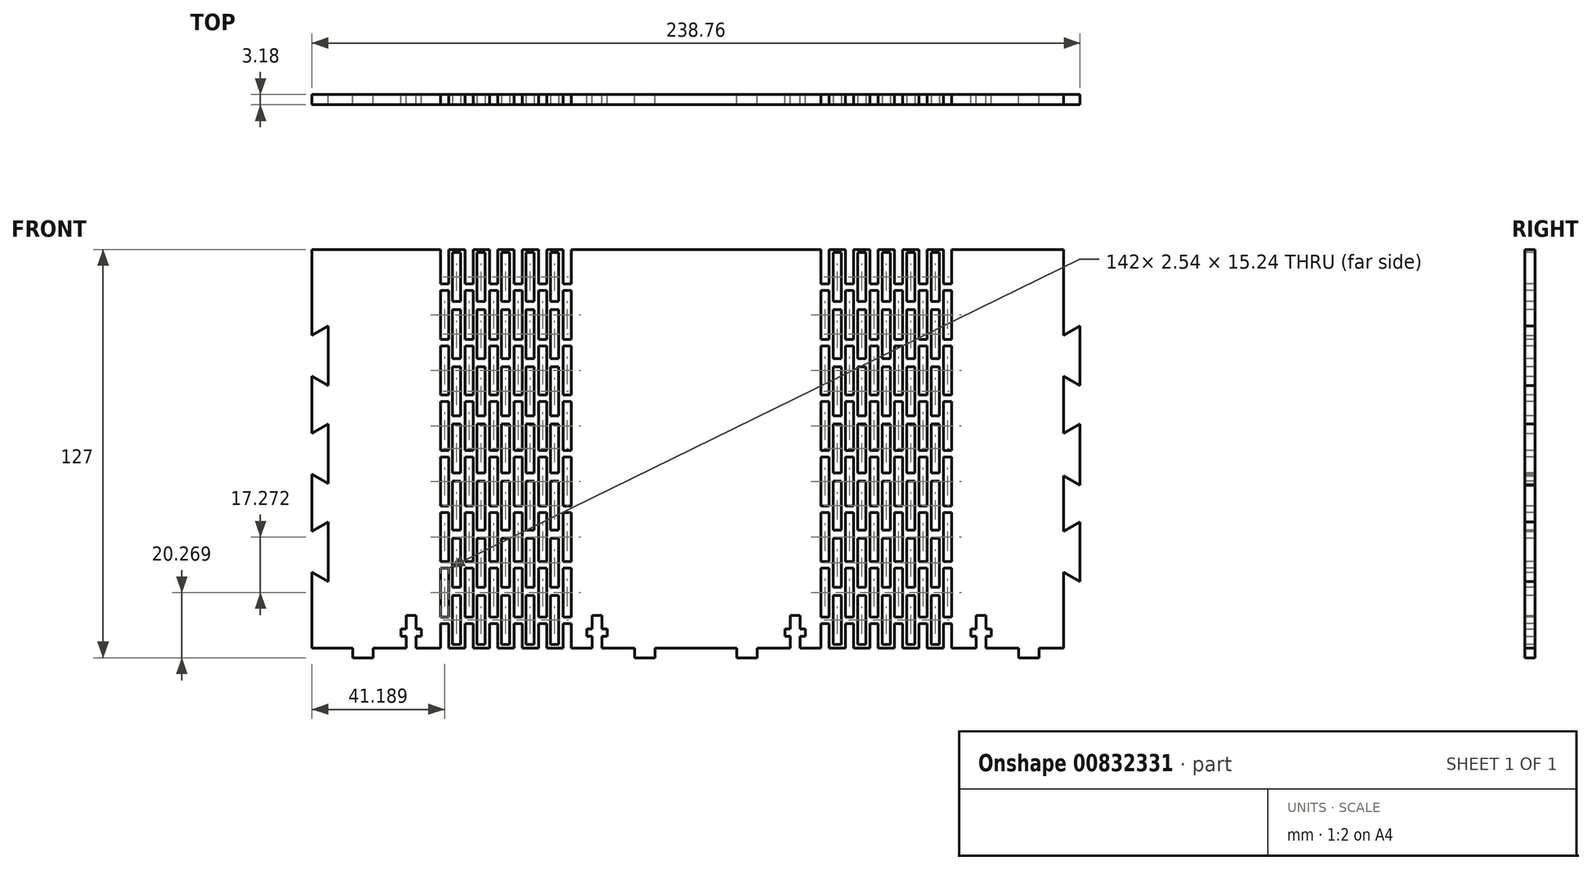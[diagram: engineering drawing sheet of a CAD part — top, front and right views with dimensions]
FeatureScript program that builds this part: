
annotation { "Feature Type Name" : "Feature", "Feature Type Description" : "" }
export const myFeature = defineFeature(function(context is Context, id is Id, definition is map)
    precondition{}
    {
        {
            var Q0;
            Q0=qCreatedBy(makeId("Front.planeOp"),FACE);
            var sketch = newSketch(context, id + "F0", { "sketchPlane" : qUnion([Q0])});
            skLineSegment(sketch, "E0.top", {"start": v(19.05, -63.5) * mm, "end": v(12.7, -63.5) * mm});
            skLineSegment(sketch, "E0.left", {"start": v(119.38, 39.76) * mm, "end": v(119.38, 21.2) * mm});
            skLineSegment(sketch, "E0.right", {"start": v(-119.38, 63.5) * mm, "end": v(-119.38, 36.83) * mm});
            skPoint(sketch, "E0.middle", {"position": v(0, 0) * mm});
            skLineSegment(sketch, "E1", {"start": v(-12.7, -60.5) * mm, "end": v(-12.7, -63.5) * mm});
            skLineSegment(sketch, "E2", {"start": v(-19.05, -60.5) * mm, "end": v(-19.05, -63.5) * mm});
            skLineSegment(sketch, "E3", {"start": v(-19.05, -60.5) * mm, "end": v(-29.26, -60.5) * mm});
            skLineSegment(sketch, "E4.MirrorCS", {"start": v(12.7, -60.5) * mm, "end": v(12.7, -63.5) * mm});
            skLineSegment(sketch, "E5.MirrorCS", {"start": v(19.05, -60.5) * mm, "end": v(19.05, -63.5) * mm});
            skLineSegment(sketch, "E6.MirrorCS", {"start": v(-19.05, -63.5) * mm, "end": v(-12.7, -63.5) * mm});
            skLineSegment(sketch, "E7.trimOffspring", {"start": v(12.7, -63.5) * mm, "end": v(19.05, -63.5) * mm});
            skLineSegment(sketch, "E8.MirrorCS", {"start": v(19.05, -60.5) * mm, "end": v(29.26, -60.5) * mm});
            skLineSegment(sketch, "E9", {"start": v(-12.7, -60.5) * mm, "end": v(12.7, -60.5) * mm});
            skLineSegment(sketch, "E10.trimOffspring", {"start": v(-12.7, -63.5) * mm, "end": v(-19.05, -63.5) * mm});
            skLineSegment(sketch, "E11.top", {"start": v(-29.26, -50.34) * mm, "end": v(-32.3, -50.34) * mm});
            skLineSegment(sketch, "E11.left", {"start": v(-29.26, -60.5) * mm, "end": v(-29.26, -56.86) * mm});
            skLineSegment(sketch, "E11.right", {"start": v(-32.3, -60.5) * mm, "end": v(-32.3, -56.86) * mm});
            skLineSegment(sketch, "E12", {"start": v(-30.78, -61.4) * mm, "end": v(-30.78, -30.9) * mm, "construction": true});
            skPoint(sketch, "E12.startSnap0", {"position": v(-30.78, -50.34) * mm});
            skLineSegment(sketch, "E13.bottom", {"start": v(-27.6, -54.48) * mm, "end": v(-29.26, -54.48) * mm});
            skLineSegment(sketch, "E13.top", {"start": v(-27.6, -56.86) * mm, "end": v(-29.26, -56.86) * mm});
            skLineSegment(sketch, "E13.left", {"start": v(-27.6, -54.48) * mm, "end": v(-27.6, -56.86) * mm});
            skLineSegment(sketch, "E13.right", {"start": v(-33.96, -54.48) * mm, "end": v(-33.96, -56.86) * mm});
            skPoint(sketch, "E13.middle", {"position": v(-30.78, -55.67) * mm});
            skLineSegment(sketch, "E14.trimOffspring", {"start": v(-32.3, -54.48) * mm, "end": v(-32.3, -50.34) * mm});
            skLineSegment(sketch, "E15.trimOffspring", {"start": v(-32.3, -54.48) * mm, "end": v(-33.96, -54.48) * mm});
            skLineSegment(sketch, "E16.trimOffspring", {"start": v(-32.3, -56.86) * mm, "end": v(-33.96, -56.86) * mm});
            skLineSegment(sketch, "E17.trimOffspring", {"start": v(-29.26, -54.48) * mm, "end": v(-29.26, -50.34) * mm});
            skLineSegment(sketch, "E18.MirrorCS", {"start": v(29.26, -60.5) * mm, "end": v(29.26, -56.86) * mm});
            skLineSegment(sketch, "E19.MirrorCS", {"start": v(27.6, -56.86) * mm, "end": v(29.26, -56.86) * mm});
            skLineSegment(sketch, "E20.MirrorCS", {"start": v(27.6, -54.48) * mm, "end": v(27.6, -56.86) * mm});
            skLineSegment(sketch, "E21.MirrorCS", {"start": v(27.6, -54.48) * mm, "end": v(29.26, -54.48) * mm});
            skLineSegment(sketch, "E22.MirrorCS", {"start": v(32.3, -60.5) * mm, "end": v(32.3, -56.86) * mm});
            skLineSegment(sketch, "E23.MirrorCS", {"start": v(32.3, -56.86) * mm, "end": v(33.96, -56.86) * mm});
            skLineSegment(sketch, "E24.MirrorCS", {"start": v(33.96, -54.48) * mm, "end": v(33.96, -56.86) * mm});
            skLineSegment(sketch, "E25.MirrorCS", {"start": v(32.3, -54.48) * mm, "end": v(33.96, -54.48) * mm});
            skLineSegment(sketch, "E26.MirrorCS", {"start": v(32.3, -54.48) * mm, "end": v(32.3, -50.34) * mm});
            skLineSegment(sketch, "E27.MirrorCS", {"start": v(29.26, -50.34) * mm, "end": v(32.3, -50.34) * mm});
            skLineSegment(sketch, "E28.MirrorCS", {"start": v(29.26, -54.48) * mm, "end": v(29.26, -50.34) * mm});
            skLineSegment(sketch, "E29.trimOffspring", {"start": v(32.3, -60.5) * mm, "end": v(87.07, -60.5) * mm});
            skLineSegment(sketch, "E30.MirrorCS", {"start": v(114.3, 63.5) * mm, "end": v(114.3, -66.28) * mm, "construction": true});
            skLineSegment(sketch, "E31", {"start": v(-119.38, 6.35) * mm, "end": v(-114.3, 9.28) * mm});
            skLineSegment(sketch, "E32.MirrorCS", {"start": v(-119.38, -6.35) * mm, "end": v(-114.3, -9.28) * mm});
            skPoint(sketch, "E33", {"position": v(-114.3, -1.4) * mm});
            skLineSegment(sketch, "E34.0.1.0", {"start": v(-119.38, 36.83) * mm, "end": v(-114.3, 39.76) * mm});
            skLineSegment(sketch, "E34.0.1.1", {"start": v(-119.38, 24.13) * mm, "end": v(-114.3, 21.2) * mm});
            skLineSegment(sketch, "E34.direction1", {"start": v(-119.38, 6.35) * mm, "end": v(-93.98, 6.35) * mm, "construction": true});
            skLineSegment(sketch, "E35.MirrorCS", {"start": v(-100.33, -60.5) * mm, "end": v(-100.33, -63.5) * mm});
            skLineSegment(sketch, "E36.MirrorCS", {"start": v(-106.68, -63.5) * mm, "end": v(-100.33, -63.5) * mm});
            skLineSegment(sketch, "E37.MirrorCS", {"start": v(-106.68, -60.5) * mm, "end": v(-106.68, -63.5) * mm});
            skLineSegment(sketch, "E38.MirrorCS", {"start": v(-90.12, -60.5) * mm, "end": v(-90.12, -56.86) * mm});
            skLineSegment(sketch, "E39.MirrorCS", {"start": v(-87.07, -60.5) * mm, "end": v(-87.07, -56.86) * mm});
            skLineSegment(sketch, "E40.MirrorCS", {"start": v(-87.07, -56.86) * mm, "end": v(-85.42, -56.86) * mm});
            skLineSegment(sketch, "E41.MirrorCS", {"start": v(-85.42, -54.48) * mm, "end": v(-85.42, -56.86) * mm});
            skLineSegment(sketch, "E42.MirrorCS", {"start": v(-87.07, -54.48) * mm, "end": v(-85.42, -54.48) * mm});
            skLineSegment(sketch, "E43.MirrorCS", {"start": v(-87.07, -54.48) * mm, "end": v(-87.07, -50.34) * mm});
            skLineSegment(sketch, "E44.MirrorCS", {"start": v(-90.12, -50.34) * mm, "end": v(-87.07, -50.34) * mm});
            skLineSegment(sketch, "E45.MirrorCS", {"start": v(-90.12, -54.48) * mm, "end": v(-90.12, -50.34) * mm});
            skLineSegment(sketch, "E46.MirrorCS", {"start": v(-91.77, -54.48) * mm, "end": v(-90.12, -54.48) * mm});
            skLineSegment(sketch, "E47.MirrorCS", {"start": v(-91.77, -54.48) * mm, "end": v(-91.77, -56.86) * mm});
            skLineSegment(sketch, "E48.MirrorCS", {"start": v(-91.77, -56.86) * mm, "end": v(-90.12, -56.86) * mm});
            skLineSegment(sketch, "E49.trimOffspring", {"start": v(-90.12, -60.5) * mm, "end": v(-100.33, -60.5) * mm});
            skLineSegment(sketch, "E50.trimOffspring", {"start": v(-106.68, -60.5) * mm, "end": v(-119.38, -60.5) * mm});
            skLineSegment(sketch, "E51.MirrorCS", {"start": v(-119.38, -24.13) * mm, "end": v(-114.3, -21.2) * mm});
            skLineSegment(sketch, "E52.MirrorCS", {"start": v(-119.38, -36.83) * mm, "end": v(-114.3, -39.76) * mm});
            skLineSegment(sketch, "E53", {"start": v(-114.3, 39.76) * mm, "end": v(-114.3, 21.2) * mm});
            skLineSegment(sketch, "E54", {"start": v(-114.3, -39.76) * mm, "end": v(-114.3, -21.2) * mm});
            skLineSegment(sketch, "E55", {"start": v(-114.3, 9.28) * mm, "end": v(-114.3, -9.28) * mm});
            skLineSegment(sketch, "E56.trimOffspring", {"start": v(-119.38, 24.13) * mm, "end": v(-119.38, 6.35) * mm});
            skLineSegment(sketch, "E57.trimOffspring", {"start": v(-119.38, -6.35) * mm, "end": v(-119.38, -24.13) * mm});
            skLineSegment(sketch, "E58.trimOffspring", {"start": v(-119.38, -36.83) * mm, "end": v(-119.38, -60.5) * mm});
            skLineSegment(sketch, "E59.1.0.0", {"start": v(114.3, 36.83) * mm, "end": v(119.38, 39.76) * mm});
            skLineSegment(sketch, "E59.1.0.2", {"start": v(114.3, 24.13) * mm, "end": v(119.38, 21.2) * mm});
            skLineSegment(sketch, "E59.direction1", {"start": v(-119.38, 36.83) * mm, "end": v(114.3, 36.83) * mm, "construction": true});
            skLineSegment(sketch, "E60", {"start": v(114.3, 36.83) * mm, "end": v(114.3, 63.5) * mm});
            skLineSegment(sketch, "E61.1.0.0", {"start": v(114.3, 6.35) * mm, "end": v(119.38, 9.28) * mm});
            skLineSegment(sketch, "E61.1.0.1", {"start": v(119.38, 9.28) * mm, "end": v(119.38, -9.28) * mm});
            skLineSegment(sketch, "E61.1.0.2", {"start": v(114.3, -6.96) * mm, "end": v(119.38, -9.9) * mm});
            skLineSegment(sketch, "E61.direction1", {"start": v(-119.38, 6.35) * mm, "end": v(114.3, 6.35) * mm, "construction": true});
            skLineSegment(sketch, "E62", {"start": v(114.3, 24.13) * mm, "end": v(114.3, 6.35) * mm});
            skLineSegment(sketch, "E63.1.0.0", {"start": v(119.38, -39.76) * mm, "end": v(119.38, -21.2) * mm});
            skLineSegment(sketch, "E63.1.0.1", {"start": v(114.3, -24.13) * mm, "end": v(119.38, -21.2) * mm});
            skLineSegment(sketch, "E63.1.0.2", {"start": v(114.3, -36.83) * mm, "end": v(119.38, -39.76) * mm});
            skLineSegment(sketch, "E63.direction1", {"start": v(-114.3, -39.76) * mm, "end": v(119.38, -39.76) * mm, "construction": true});
            skLineSegment(sketch, "E64", {"start": v(114.3, -24.13) * mm, "end": v(114.3, -6.96) * mm});
            skLineSegment(sketch, "E65", {"start": v(114.3, -60.5) * mm, "end": v(114.3, -36.83) * mm});
            skLineSegment(sketch, "E66.trimOffspring", {"start": v(119.38, -21.2) * mm, "end": v(119.38, -39.76) * mm});
            skLineSegment(sketch, "E67.MirrorCS", {"start": v(87.07, -60.5) * mm, "end": v(87.07, -56.86) * mm});
            skLineSegment(sketch, "E68.MirrorCS", {"start": v(87.07, -56.86) * mm, "end": v(85.42, -56.86) * mm});
            skLineSegment(sketch, "E69.MirrorCS", {"start": v(85.42, -54.48) * mm, "end": v(85.42, -56.86) * mm});
            skLineSegment(sketch, "E70.MirrorCS", {"start": v(87.07, -54.48) * mm, "end": v(85.42, -54.48) * mm});
            skLineSegment(sketch, "E71.MirrorCS", {"start": v(87.07, -54.48) * mm, "end": v(87.07, -50.34) * mm});
            skLineSegment(sketch, "E72.MirrorCS", {"start": v(90.12, -50.34) * mm, "end": v(87.07, -50.34) * mm});
            skLineSegment(sketch, "E73.MirrorCS", {"start": v(90.12, -54.48) * mm, "end": v(90.12, -50.34) * mm});
            skLineSegment(sketch, "E74.MirrorCS", {"start": v(91.77, -54.48) * mm, "end": v(90.12, -54.48) * mm});
            skLineSegment(sketch, "E75.MirrorCS", {"start": v(91.77, -54.48) * mm, "end": v(91.77, -56.86) * mm});
            skLineSegment(sketch, "E76.MirrorCS", {"start": v(91.77, -56.86) * mm, "end": v(90.12, -56.86) * mm});
            skLineSegment(sketch, "E77.MirrorCS", {"start": v(90.12, -60.5) * mm, "end": v(90.12, -56.86) * mm});
            skLineSegment(sketch, "E78.MirrorCS", {"start": v(106.68, -60.5) * mm, "end": v(106.68, -63.5) * mm});
            skLineSegment(sketch, "E79.MirrorCS", {"start": v(106.68, -63.5) * mm, "end": v(100.33, -63.5) * mm});
            skLineSegment(sketch, "E80.MirrorCS", {"start": v(100.33, -60.5) * mm, "end": v(100.33, -63.5) * mm});
            skLineSegment(sketch, "E81.trimOffspring", {"start": v(90.12, -60.5) * mm, "end": v(100.33, -60.5) * mm});
            skLineSegment(sketch, "E82.trimOffspring", {"start": v(106.68, -60.5) * mm, "end": v(114.3, -60.5) * mm});
            skLineSegment(sketch, "E83", {"start": v(119.38, -9.9) * mm, "end": v(119.38, -9.28) * mm});
            skLineSegment(sketch, "E84", {"start": v(-87.07, -60.5) * mm, "end": v(-32.3, -60.5) * mm});
            skLineSegment(sketch, "E85", {"start": v(-119.38, 63.5) * mm, "end": v(114.3, 63.5) * mm});
            skSolve(sketch);
        }
        {
            var Q0;
            Q0 = qSketchRegion(id + "F0", true);
            extrude(context, id + "F1", {"entities" : qUnion([Q0]), "depth" : 3.17 * mm, "offsetDistance" : 25.4 * mm});
        }
        {
            var Q0;
            Q0=makeQuery(id+"F1.opExtrude","CAP_FACE",FACE,{"disambiguationData":[OSD([sQuery(id+"F0.wireOp",EDGE,"E0.right"),sQuery(id+"F0.wireOp",EDGE,"E1"),sQuery(id+"F0.wireOp",EDGE,"E2"),sQuery(id+"F0.wireOp",EDGE,"E3"),sQuery(id+"F0.wireOp",EDGE,"E4.MirrorCS"),sQuery(id+"F0.wireOp",EDGE,"E5.MirrorCS"),sQuery(id+"F0.wireOp",EDGE,"E7.trimOffspring"),sQuery(id+"F0.wireOp",EDGE,"E8.MirrorCS"),sQuery(id+"F0.wireOp",EDGE,"E9"),sQuery(id+"F0.wireOp",EDGE,"E10.trimOffspring"),sQuery(id+"F0.wireOp",EDGE,"E11.top"),sQuery(id+"F0.wireOp",EDGE,"E11.left"),sQuery(id+"F0.wireOp",EDGE,"E11.right"),sQuery(id+"F0.wireOp",EDGE,"E13.bottom"),sQuery(id+"F0.wireOp",EDGE,"E13.top"),sQuery(id+"F0.wireOp",EDGE,"E13.left"),sQuery(id+"F0.wireOp",EDGE,"E13.right"),sQuery(id+"F0.wireOp",EDGE,"E14.trimOffspring"),sQuery(id+"F0.wireOp",EDGE,"E15.trimOffspring"),sQuery(id+"F0.wireOp",EDGE,"E16.trimOffspring"),sQuery(id+"F0.wireOp",EDGE,"E17.trimOffspring"),sQuery(id+"F0.wireOp",EDGE,"E18.MirrorCS"),sQuery(id+"F0.wireOp",EDGE,"E19.MirrorCS"),sQuery(id+"F0.wireOp",EDGE,"E20.MirrorCS"),sQuery(id+"F0.wireOp",EDGE,"E21.MirrorCS"),sQuery(id+"F0.wireOp",EDGE,"E22.MirrorCS"),sQuery(id+"F0.wireOp",EDGE,"E23.MirrorCS"),sQuery(id+"F0.wireOp",EDGE,"E24.MirrorCS"),sQuery(id+"F0.wireOp",EDGE,"E25.MirrorCS"),sQuery(id+"F0.wireOp",EDGE,"E26.MirrorCS"),sQuery(id+"F0.wireOp",EDGE,"E27.MirrorCS"),sQuery(id+"F0.wireOp",EDGE,"E28.MirrorCS"),sQuery(id+"F0.wireOp",EDGE,"E29.trimOffspring"),sQuery(id+"F0.wireOp",EDGE,"E31"),sQuery(id+"F0.wireOp",EDGE,"E32.MirrorCS"),sQuery(id+"F0.wireOp",EDGE,"E34.0.1.0"),sQuery(id+"F0.wireOp",EDGE,"E34.0.1.1"),sQuery(id+"F0.wireOp",EDGE,"E35.MirrorCS"),sQuery(id+"F0.wireOp",EDGE,"E36.MirrorCS"),sQuery(id+"F0.wireOp",EDGE,"E37.MirrorCS"),sQuery(id+"F0.wireOp",EDGE,"E39.MirrorCS"),sQuery(id+"F0.wireOp",EDGE,"E40.MirrorCS"),sQuery(id+"F0.wireOp",EDGE,"E41.MirrorCS"),sQuery(id+"F0.wireOp",EDGE,"E42.MirrorCS"),sQuery(id+"F0.wireOp",EDGE,"E43.MirrorCS"),sQuery(id+"F0.wireOp",EDGE,"E44.MirrorCS"),sQuery(id+"F0.wireOp",EDGE,"E45.MirrorCS"),sQuery(id+"F0.wireOp",EDGE,"E46.MirrorCS"),sQuery(id+"F0.wireOp",EDGE,"E47.MirrorCS"),sQuery(id+"F0.wireOp",EDGE,"E48.MirrorCS"),sQuery(id+"F0.wireOp",EDGE,"E38.MirrorCS"),sQuery(id+"F0.wireOp",EDGE,"E49.trimOffspring"),sQuery(id+"F0.wireOp",EDGE,"E50.trimOffspring"),sQuery(id+"F0.wireOp",EDGE,"E51.MirrorCS"),sQuery(id+"F0.wireOp",EDGE,"E52.MirrorCS"),sQuery(id+"F0.wireOp",EDGE,"E53"),sQuery(id+"F0.wireOp",EDGE,"E54"),sQuery(id+"F0.wireOp",EDGE,"E55"),sQuery(id+"F0.wireOp",EDGE,"E56.trimOffspring"),sQuery(id+"F0.wireOp",EDGE,"E57.trimOffspring"),sQuery(id+"F0.wireOp",EDGE,"E58.trimOffspring"),sQuery(id+"F0.wireOp",EDGE,"E59.1.0.0"),sQuery(id+"F0.wireOp",EDGE,"E0.left"),sQuery(id+"F0.wireOp",EDGE,"E59.1.0.2"),sQuery(id+"F0.wireOp",EDGE,"E60"),sQuery(id+"F0.wireOp",EDGE,"E61.1.0.0"),sQuery(id+"F0.wireOp",EDGE,"E61.1.0.2"),sQuery(id+"F0.wireOp",EDGE,"E62"),sQuery(id+"F0.wireOp",EDGE,"E61.1.0.1"),sQuery(id+"F0.wireOp",EDGE,"E63.1.0.1"),sQuery(id+"F0.wireOp",EDGE,"E63.1.0.2"),sQuery(id+"F0.wireOp",EDGE,"E64"),sQuery(id+"F0.wireOp",EDGE,"E65"),sQuery(id+"F0.wireOp",EDGE,"E66.trimOffspring"),sQuery(id+"F0.wireOp",EDGE,"E67.MirrorCS"),sQuery(id+"F0.wireOp",EDGE,"E68.MirrorCS"),sQuery(id+"F0.wireOp",EDGE,"E69.MirrorCS"),sQuery(id+"F0.wireOp",EDGE,"E70.MirrorCS"),sQuery(id+"F0.wireOp",EDGE,"E71.MirrorCS"),sQuery(id+"F0.wireOp",EDGE,"E72.MirrorCS"),sQuery(id+"F0.wireOp",EDGE,"E73.MirrorCS"),sQuery(id+"F0.wireOp",EDGE,"E74.MirrorCS"),sQuery(id+"F0.wireOp",EDGE,"E75.MirrorCS"),sQuery(id+"F0.wireOp",EDGE,"E76.MirrorCS"),sQuery(id+"F0.wireOp",EDGE,"E77.MirrorCS"),sQuery(id+"F0.wireOp",EDGE,"E78.MirrorCS"),sQuery(id+"F0.wireOp",EDGE,"E79.MirrorCS"),sQuery(id+"F0.wireOp",EDGE,"E80.MirrorCS"),sQuery(id+"F0.wireOp",EDGE,"E81.trimOffspring"),sQuery(id+"F0.wireOp",EDGE,"E82.trimOffspring"),sQuery(id+"F0.wireOp",EDGE,"E83"),sQuery(id+"F0.wireOp",EDGE,"E84"),sQuery(id+"F0.wireOp",EDGE,"E85")])],"isStart":false});
            var sketch = newSketch(context, id + "F2", { "sketchPlane" : qUnion([Q0])});
            skLineSegment(sketch, "E86", {"start": v(-38.22, -63.67) * mm, "end": v(-38.22, 65.15) * mm, "construction": true});
            skLineSegment(sketch, "E87.1.0.0", {"start": v(-42.03, -63.67) * mm, "end": v(-42.03, 65.15) * mm, "construction": true});
            skLineSegment(sketch, "E87.2.0.0", {"start": v(-45.84, -63.67) * mm, "end": v(-45.84, 65.15) * mm, "construction": true});
            skLineSegment(sketch, "E87.3.0.0", {"start": v(-49.65, -63.67) * mm, "end": v(-49.65, 65.15) * mm, "construction": true});
            skLineSegment(sketch, "E87.4.0.0", {"start": v(-53.46, -63.67) * mm, "end": v(-53.46, 65.15) * mm, "construction": true});
            skLineSegment(sketch, "E87.5.0.0", {"start": v(-57.27, -63.67) * mm, "end": v(-57.27, 65.15) * mm, "construction": true});
            skLineSegment(sketch, "E87.6.0.0", {"start": v(-61.08, -63.67) * mm, "end": v(-61.08, 65.15) * mm, "construction": true});
            skLineSegment(sketch, "E87.7.0.0", {"start": v(-64.89, -63.67) * mm, "end": v(-64.89, 65.15) * mm, "construction": true});
            skLineSegment(sketch, "E87.8.0.0", {"start": v(-68.7, -63.67) * mm, "end": v(-68.7, 65.15) * mm, "construction": true});
            skLineSegment(sketch, "E87.9.0.0", {"start": v(-72.5, -63.67) * mm, "end": v(-72.5, 65.15) * mm, "construction": true});
            skLineSegment(sketch, "E87.10.0.0", {"start": v(-76.32, -63.67) * mm, "end": v(-76.32, 65.15) * mm, "construction": true});
            skLineSegment(sketch, "E87.11.0.0", {"start": v(-80.13, -63.67) * mm, "end": v(-80.13, 65.15) * mm, "construction": true});
            skLineSegment(sketch, "E87.direction1", {"start": v(-38.22, -63.67) * mm, "end": v(-42.03, -63.67) * mm, "construction": true});
            skLineSegment(sketch, "E88.bottom", {"start": v(-38.82, -52.88) * mm, "end": v(-41.36, -52.88) * mm});
            skLineSegment(sketch, "E88.left", {"start": v(-38.82, -52.88) * mm, "end": v(-38.82, -60.5) * mm});
            skLineSegment(sketch, "E88.right", {"start": v(-41.36, -52.88) * mm, "end": v(-41.36, -60.5) * mm});
            skPoint(sketch, "E88.middle", {"position": v(-40.1, -60.5) * mm});
            skLineSegment(sketch, "E89.0.1.0", {"start": v(-38.82, -35.61) * mm, "end": v(-38.82, -50.85) * mm});
            skPoint(sketch, "E89.0.1.1", {"position": v(-40.1, -43.23) * mm});
            skLineSegment(sketch, "E89.0.1.2", {"start": v(-38.82, -50.85) * mm, "end": v(-41.36, -50.85) * mm});
            skLineSegment(sketch, "E89.0.1.3", {"start": v(-38.82, -35.61) * mm, "end": v(-41.36, -35.61) * mm});
            skLineSegment(sketch, "E89.0.1.4", {"start": v(-41.36, -35.61) * mm, "end": v(-41.36, -50.85) * mm});
            skLineSegment(sketch, "E89.0.2.0", {"start": v(-38.82, -18.34) * mm, "end": v(-38.82, -33.58) * mm});
            skPoint(sketch, "E89.0.2.1", {"position": v(-40.1, -25.96) * mm});
            skLineSegment(sketch, "E89.0.2.2", {"start": v(-38.82, -33.58) * mm, "end": v(-41.36, -33.58) * mm});
            skLineSegment(sketch, "E89.0.2.3", {"start": v(-38.82, -18.34) * mm, "end": v(-41.36, -18.34) * mm});
            skLineSegment(sketch, "E89.0.2.4", {"start": v(-41.36, -18.34) * mm, "end": v(-41.36, -33.58) * mm});
            skLineSegment(sketch, "E89.0.3.0", {"start": v(-38.82, -1.07) * mm, "end": v(-38.82, -16.3) * mm});
            skPoint(sketch, "E89.0.3.1", {"position": v(-40.1, -8.69) * mm});
            skLineSegment(sketch, "E89.0.3.2", {"start": v(-38.82, -16.3) * mm, "end": v(-41.36, -16.3) * mm});
            skLineSegment(sketch, "E89.0.3.3", {"start": v(-38.82, -1.07) * mm, "end": v(-41.36, -1.07) * mm});
            skLineSegment(sketch, "E89.0.3.4", {"start": v(-41.36, -1.07) * mm, "end": v(-41.36, -16.3) * mm});
            skLineSegment(sketch, "E89.0.4.0", {"start": v(-38.82, 16.2) * mm, "end": v(-38.82, 0.97) * mm});
            skPoint(sketch, "E89.0.4.1", {"position": v(-40.1, 8.59) * mm});
            skLineSegment(sketch, "E89.0.4.2", {"start": v(-38.82, 0.97) * mm, "end": v(-41.36, 0.97) * mm});
            skLineSegment(sketch, "E89.0.4.3", {"start": v(-38.82, 16.2) * mm, "end": v(-41.36, 16.2) * mm});
            skLineSegment(sketch, "E89.0.4.4", {"start": v(-41.36, 16.2) * mm, "end": v(-41.36, 0.97) * mm});
            skLineSegment(sketch, "E89.0.5.0", {"start": v(-38.82, 33.48) * mm, "end": v(-38.82, 18.24) * mm});
            skPoint(sketch, "E89.0.5.1", {"position": v(-40.1, 25.86) * mm});
            skLineSegment(sketch, "E89.0.5.2", {"start": v(-38.82, 18.24) * mm, "end": v(-41.36, 18.24) * mm});
            skLineSegment(sketch, "E89.0.5.3", {"start": v(-38.82, 33.48) * mm, "end": v(-41.36, 33.48) * mm});
            skLineSegment(sketch, "E89.0.5.4", {"start": v(-41.36, 33.48) * mm, "end": v(-41.36, 18.24) * mm});
            skLineSegment(sketch, "E89.0.6.0", {"start": v(-38.82, 50.75) * mm, "end": v(-38.82, 35.5) * mm});
            skPoint(sketch, "E89.0.6.1", {"position": v(-40.1, 43.13) * mm});
            skLineSegment(sketch, "E89.0.6.2", {"start": v(-38.82, 35.5) * mm, "end": v(-41.36, 35.5) * mm});
            skLineSegment(sketch, "E89.0.6.3", {"start": v(-38.82, 50.75) * mm, "end": v(-41.36, 50.75) * mm});
            skLineSegment(sketch, "E89.0.6.4", {"start": v(-41.36, 50.75) * mm, "end": v(-41.36, 35.5) * mm});
            skLineSegment(sketch, "E89.0.7.0", {"start": v(-38.82, 63.5) * mm, "end": v(-38.82, 52.78) * mm});
            skPoint(sketch, "E89.0.7.1", {"position": v(-40.1, 60.4) * mm});
            skLineSegment(sketch, "E89.0.7.2", {"start": v(-38.82, 52.78) * mm, "end": v(-41.36, 52.78) * mm});
            skLineSegment(sketch, "E89.0.7.4", {"start": v(-41.36, 63.5) * mm, "end": v(-41.36, 52.78) * mm});
            skLineSegment(sketch, "E89.1.0.0", {"start": v(-46.44, -52.88) * mm, "end": v(-46.44, -60.5) * mm});
            skPoint(sketch, "E89.1.0.1", {"position": v(-47.71, -60.5) * mm});
            skLineSegment(sketch, "E89.1.0.3", {"start": v(-46.44, -52.88) * mm, "end": v(-48.98, -52.88) * mm});
            skLineSegment(sketch, "E89.1.0.4", {"start": v(-48.98, -52.88) * mm, "end": v(-48.98, -60.5) * mm});
            skLineSegment(sketch, "E89.1.1.0", {"start": v(-46.44, -35.61) * mm, "end": v(-46.44, -50.85) * mm});
            skPoint(sketch, "E89.1.1.1", {"position": v(-47.71, -43.23) * mm});
            skLineSegment(sketch, "E89.1.1.2", {"start": v(-46.44, -50.85) * mm, "end": v(-48.98, -50.85) * mm});
            skLineSegment(sketch, "E89.1.1.3", {"start": v(-46.44, -35.61) * mm, "end": v(-48.98, -35.61) * mm});
            skLineSegment(sketch, "E89.1.1.4", {"start": v(-48.98, -35.61) * mm, "end": v(-48.98, -50.85) * mm});
            skLineSegment(sketch, "E89.1.2.0", {"start": v(-46.44, -18.34) * mm, "end": v(-46.44, -33.58) * mm});
            skPoint(sketch, "E89.1.2.1", {"position": v(-47.71, -25.96) * mm});
            skLineSegment(sketch, "E89.1.2.2", {"start": v(-46.44, -33.58) * mm, "end": v(-48.98, -33.58) * mm});
            skLineSegment(sketch, "E89.1.2.3", {"start": v(-46.44, -18.34) * mm, "end": v(-48.98, -18.34) * mm});
            skLineSegment(sketch, "E89.1.2.4", {"start": v(-48.98, -18.34) * mm, "end": v(-48.98, -33.58) * mm});
            skLineSegment(sketch, "E89.1.3.0", {"start": v(-46.44, -1.07) * mm, "end": v(-46.44, -16.3) * mm});
            skPoint(sketch, "E89.1.3.1", {"position": v(-47.71, -8.69) * mm});
            skLineSegment(sketch, "E89.1.3.2", {"start": v(-46.44, -16.3) * mm, "end": v(-48.98, -16.3) * mm});
            skLineSegment(sketch, "E89.1.3.3", {"start": v(-46.44, -1.07) * mm, "end": v(-48.98, -1.07) * mm});
            skLineSegment(sketch, "E89.1.3.4", {"start": v(-48.98, -1.07) * mm, "end": v(-48.98, -16.3) * mm});
            skLineSegment(sketch, "E89.1.4.0", {"start": v(-46.44, 16.2) * mm, "end": v(-46.44, 0.97) * mm});
            skPoint(sketch, "E89.1.4.1", {"position": v(-47.71, 8.59) * mm});
            skLineSegment(sketch, "E89.1.4.2", {"start": v(-46.44, 0.97) * mm, "end": v(-48.98, 0.97) * mm});
            skLineSegment(sketch, "E89.1.4.3", {"start": v(-46.44, 16.2) * mm, "end": v(-48.98, 16.2) * mm});
            skLineSegment(sketch, "E89.1.4.4", {"start": v(-48.98, 16.2) * mm, "end": v(-48.98, 0.97) * mm});
            skLineSegment(sketch, "E89.1.5.0", {"start": v(-46.44, 33.48) * mm, "end": v(-46.44, 18.24) * mm});
            skPoint(sketch, "E89.1.5.1", {"position": v(-47.71, 25.86) * mm});
            skLineSegment(sketch, "E89.1.5.2", {"start": v(-46.44, 18.24) * mm, "end": v(-48.98, 18.24) * mm});
            skLineSegment(sketch, "E89.1.5.3", {"start": v(-46.44, 33.48) * mm, "end": v(-48.98, 33.48) * mm});
            skLineSegment(sketch, "E89.1.5.4", {"start": v(-48.98, 33.48) * mm, "end": v(-48.98, 18.24) * mm});
            skLineSegment(sketch, "E89.1.6.0", {"start": v(-46.44, 50.75) * mm, "end": v(-46.44, 35.5) * mm});
            skPoint(sketch, "E89.1.6.1", {"position": v(-47.71, 43.13) * mm});
            skLineSegment(sketch, "E89.1.6.2", {"start": v(-46.44, 35.5) * mm, "end": v(-48.98, 35.5) * mm});
            skLineSegment(sketch, "E89.1.6.3", {"start": v(-46.44, 50.75) * mm, "end": v(-48.98, 50.75) * mm});
            skLineSegment(sketch, "E89.1.6.4", {"start": v(-48.98, 50.75) * mm, "end": v(-48.98, 35.5) * mm});
            skLineSegment(sketch, "E89.1.7.0", {"start": v(-46.44, 63.5) * mm, "end": v(-46.44, 52.78) * mm});
            skPoint(sketch, "E89.1.7.1", {"position": v(-47.71, 60.4) * mm});
            skLineSegment(sketch, "E89.1.7.2", {"start": v(-46.44, 52.78) * mm, "end": v(-48.98, 52.78) * mm});
            skLineSegment(sketch, "E89.1.7.4", {"start": v(-48.98, 63.5) * mm, "end": v(-48.98, 52.78) * mm});
            skLineSegment(sketch, "E89.2.0.0", {"start": v(-54.06, -52.88) * mm, "end": v(-54.06, -60.5) * mm});
            skPoint(sketch, "E89.2.0.1", {"position": v(-55.33, -60.5) * mm});
            skLineSegment(sketch, "E89.2.0.3", {"start": v(-54.06, -52.88) * mm, "end": v(-56.6, -52.88) * mm});
            skLineSegment(sketch, "E89.2.0.4", {"start": v(-56.6, -52.88) * mm, "end": v(-56.6, -60.5) * mm});
            skLineSegment(sketch, "E89.2.1.0", {"start": v(-54.06, -35.61) * mm, "end": v(-54.06, -50.85) * mm});
            skPoint(sketch, "E89.2.1.1", {"position": v(-55.33, -43.23) * mm});
            skLineSegment(sketch, "E89.2.1.2", {"start": v(-54.06, -50.85) * mm, "end": v(-56.6, -50.85) * mm});
            skLineSegment(sketch, "E89.2.1.3", {"start": v(-54.06, -35.61) * mm, "end": v(-56.6, -35.61) * mm});
            skLineSegment(sketch, "E89.2.1.4", {"start": v(-56.6, -35.61) * mm, "end": v(-56.6, -50.85) * mm});
            skLineSegment(sketch, "E89.2.2.0", {"start": v(-54.06, -18.34) * mm, "end": v(-54.06, -33.58) * mm});
            skPoint(sketch, "E89.2.2.1", {"position": v(-55.33, -25.96) * mm});
            skLineSegment(sketch, "E89.2.2.2", {"start": v(-54.06, -33.58) * mm, "end": v(-56.6, -33.58) * mm});
            skLineSegment(sketch, "E89.2.2.3", {"start": v(-54.06, -18.34) * mm, "end": v(-56.6, -18.34) * mm});
            skLineSegment(sketch, "E89.2.2.4", {"start": v(-56.6, -18.34) * mm, "end": v(-56.6, -33.58) * mm});
            skLineSegment(sketch, "E89.2.3.0", {"start": v(-54.06, -1.07) * mm, "end": v(-54.06, -16.3) * mm});
            skPoint(sketch, "E89.2.3.1", {"position": v(-55.33, -8.69) * mm});
            skLineSegment(sketch, "E89.2.3.2", {"start": v(-54.06, -16.3) * mm, "end": v(-56.6, -16.3) * mm});
            skLineSegment(sketch, "E89.2.3.3", {"start": v(-54.06, -1.07) * mm, "end": v(-56.6, -1.07) * mm});
            skLineSegment(sketch, "E89.2.3.4", {"start": v(-56.6, -1.07) * mm, "end": v(-56.6, -16.3) * mm});
            skLineSegment(sketch, "E89.2.4.0", {"start": v(-54.06, 16.2) * mm, "end": v(-54.06, 0.97) * mm});
            skPoint(sketch, "E89.2.4.1", {"position": v(-55.33, 8.59) * mm});
            skLineSegment(sketch, "E89.2.4.2", {"start": v(-54.06, 0.97) * mm, "end": v(-56.6, 0.97) * mm});
            skLineSegment(sketch, "E89.2.4.3", {"start": v(-54.06, 16.2) * mm, "end": v(-56.6, 16.2) * mm});
            skLineSegment(sketch, "E89.2.4.4", {"start": v(-56.6, 16.2) * mm, "end": v(-56.6, 0.97) * mm});
            skLineSegment(sketch, "E89.2.5.0", {"start": v(-54.06, 33.48) * mm, "end": v(-54.06, 18.24) * mm});
            skPoint(sketch, "E89.2.5.1", {"position": v(-55.33, 25.86) * mm});
            skLineSegment(sketch, "E89.2.5.2", {"start": v(-54.06, 18.24) * mm, "end": v(-56.6, 18.24) * mm});
            skLineSegment(sketch, "E89.2.5.3", {"start": v(-54.06, 33.48) * mm, "end": v(-56.6, 33.48) * mm});
            skLineSegment(sketch, "E89.2.5.4", {"start": v(-56.6, 33.48) * mm, "end": v(-56.6, 18.24) * mm});
            skLineSegment(sketch, "E89.2.6.0", {"start": v(-54.06, 50.75) * mm, "end": v(-54.06, 35.5) * mm});
            skPoint(sketch, "E89.2.6.1", {"position": v(-55.33, 43.13) * mm});
            skLineSegment(sketch, "E89.2.6.2", {"start": v(-54.06, 35.5) * mm, "end": v(-56.6, 35.5) * mm});
            skLineSegment(sketch, "E89.2.6.3", {"start": v(-54.06, 50.75) * mm, "end": v(-56.6, 50.75) * mm});
            skLineSegment(sketch, "E89.2.6.4", {"start": v(-56.6, 50.75) * mm, "end": v(-56.6, 35.5) * mm});
            skLineSegment(sketch, "E89.2.7.0", {"start": v(-54.06, 63.5) * mm, "end": v(-54.06, 52.78) * mm});
            skPoint(sketch, "E89.2.7.1", {"position": v(-55.33, 60.4) * mm});
            skLineSegment(sketch, "E89.2.7.2", {"start": v(-54.06, 52.78) * mm, "end": v(-56.6, 52.78) * mm});
            skLineSegment(sketch, "E89.2.7.4", {"start": v(-56.6, 63.5) * mm, "end": v(-56.6, 52.78) * mm});
            skLineSegment(sketch, "E89.3.0.0", {"start": v(-61.68, -52.88) * mm, "end": v(-61.68, -60.5) * mm});
            skPoint(sketch, "E89.3.0.1", {"position": v(-62.95, -60.5) * mm});
            skLineSegment(sketch, "E89.3.0.3", {"start": v(-61.68, -52.88) * mm, "end": v(-64.22, -52.88) * mm});
            skLineSegment(sketch, "E89.3.0.4", {"start": v(-64.22, -52.88) * mm, "end": v(-64.22, -60.5) * mm});
            skLineSegment(sketch, "E89.3.1.0", {"start": v(-61.68, -35.61) * mm, "end": v(-61.68, -50.85) * mm});
            skPoint(sketch, "E89.3.1.1", {"position": v(-62.95, -43.23) * mm});
            skLineSegment(sketch, "E89.3.1.2", {"start": v(-61.68, -50.85) * mm, "end": v(-64.22, -50.85) * mm});
            skLineSegment(sketch, "E89.3.1.3", {"start": v(-61.68, -35.61) * mm, "end": v(-64.22, -35.61) * mm});
            skLineSegment(sketch, "E89.3.1.4", {"start": v(-64.22, -35.61) * mm, "end": v(-64.22, -50.85) * mm});
            skLineSegment(sketch, "E89.3.2.0", {"start": v(-61.68, -18.34) * mm, "end": v(-61.68, -33.58) * mm});
            skPoint(sketch, "E89.3.2.1", {"position": v(-62.95, -25.96) * mm});
            skLineSegment(sketch, "E89.3.2.2", {"start": v(-61.68, -33.58) * mm, "end": v(-64.22, -33.58) * mm});
            skLineSegment(sketch, "E89.3.2.3", {"start": v(-61.68, -18.34) * mm, "end": v(-64.22, -18.34) * mm});
            skLineSegment(sketch, "E89.3.2.4", {"start": v(-64.22, -18.34) * mm, "end": v(-64.22, -33.58) * mm});
            skLineSegment(sketch, "E89.3.3.0", {"start": v(-61.68, -1.07) * mm, "end": v(-61.68, -16.3) * mm});
            skPoint(sketch, "E89.3.3.1", {"position": v(-62.95, -8.69) * mm});
            skLineSegment(sketch, "E89.3.3.2", {"start": v(-61.68, -16.3) * mm, "end": v(-64.22, -16.3) * mm});
            skLineSegment(sketch, "E89.3.3.3", {"start": v(-61.68, -1.07) * mm, "end": v(-64.22, -1.07) * mm});
            skLineSegment(sketch, "E89.3.3.4", {"start": v(-64.22, -1.07) * mm, "end": v(-64.22, -16.3) * mm});
            skLineSegment(sketch, "E89.3.4.0", {"start": v(-61.68, 16.2) * mm, "end": v(-61.68, 0.97) * mm});
            skPoint(sketch, "E89.3.4.1", {"position": v(-62.95, 8.59) * mm});
            skLineSegment(sketch, "E89.3.4.2", {"start": v(-61.68, 0.97) * mm, "end": v(-64.22, 0.97) * mm});
            skLineSegment(sketch, "E89.3.4.3", {"start": v(-61.68, 16.2) * mm, "end": v(-64.22, 16.2) * mm});
            skLineSegment(sketch, "E89.3.4.4", {"start": v(-64.22, 16.2) * mm, "end": v(-64.22, 0.97) * mm});
            skLineSegment(sketch, "E89.3.5.0", {"start": v(-61.68, 33.48) * mm, "end": v(-61.68, 18.24) * mm});
            skPoint(sketch, "E89.3.5.1", {"position": v(-62.95, 25.86) * mm});
            skLineSegment(sketch, "E89.3.5.2", {"start": v(-61.68, 18.24) * mm, "end": v(-64.22, 18.24) * mm});
            skLineSegment(sketch, "E89.3.5.3", {"start": v(-61.68, 33.48) * mm, "end": v(-64.22, 33.48) * mm});
            skLineSegment(sketch, "E89.3.5.4", {"start": v(-64.22, 33.48) * mm, "end": v(-64.22, 18.24) * mm});
            skLineSegment(sketch, "E89.3.6.0", {"start": v(-61.68, 50.75) * mm, "end": v(-61.68, 35.5) * mm});
            skPoint(sketch, "E89.3.6.1", {"position": v(-62.95, 43.13) * mm});
            skLineSegment(sketch, "E89.3.6.2", {"start": v(-61.68, 35.5) * mm, "end": v(-64.22, 35.5) * mm});
            skLineSegment(sketch, "E89.3.6.3", {"start": v(-61.68, 50.75) * mm, "end": v(-64.22, 50.75) * mm});
            skLineSegment(sketch, "E89.3.6.4", {"start": v(-64.22, 50.75) * mm, "end": v(-64.22, 35.5) * mm});
            skLineSegment(sketch, "E89.3.7.0", {"start": v(-61.68, 63.5) * mm, "end": v(-61.68, 52.78) * mm});
            skPoint(sketch, "E89.3.7.1", {"position": v(-62.95, 60.4) * mm});
            skLineSegment(sketch, "E89.3.7.2", {"start": v(-61.68, 52.78) * mm, "end": v(-64.22, 52.78) * mm});
            skLineSegment(sketch, "E89.3.7.4", {"start": v(-64.22, 63.5) * mm, "end": v(-64.22, 52.78) * mm});
            skLineSegment(sketch, "E89.4.0.0", {"start": v(-69.3, -52.88) * mm, "end": v(-69.3, -60.5) * mm});
            skPoint(sketch, "E89.4.0.1", {"position": v(-70.57, -60.5) * mm});
            skLineSegment(sketch, "E89.4.0.3", {"start": v(-69.3, -52.88) * mm, "end": v(-71.84, -52.88) * mm});
            skLineSegment(sketch, "E89.4.0.4", {"start": v(-71.84, -52.88) * mm, "end": v(-71.84, -60.5) * mm});
            skLineSegment(sketch, "E89.4.1.0", {"start": v(-69.3, -35.61) * mm, "end": v(-69.3, -50.85) * mm});
            skPoint(sketch, "E89.4.1.1", {"position": v(-70.57, -43.23) * mm});
            skLineSegment(sketch, "E89.4.1.2", {"start": v(-69.3, -50.85) * mm, "end": v(-71.84, -50.85) * mm});
            skLineSegment(sketch, "E89.4.1.3", {"start": v(-69.3, -35.61) * mm, "end": v(-71.84, -35.61) * mm});
            skLineSegment(sketch, "E89.4.1.4", {"start": v(-71.84, -35.61) * mm, "end": v(-71.84, -50.85) * mm});
            skLineSegment(sketch, "E89.4.2.0", {"start": v(-69.3, -18.34) * mm, "end": v(-69.3, -33.58) * mm});
            skPoint(sketch, "E89.4.2.1", {"position": v(-70.57, -25.96) * mm});
            skLineSegment(sketch, "E89.4.2.2", {"start": v(-69.3, -33.58) * mm, "end": v(-71.84, -33.58) * mm});
            skLineSegment(sketch, "E89.4.2.3", {"start": v(-69.3, -18.34) * mm, "end": v(-71.84, -18.34) * mm});
            skLineSegment(sketch, "E89.4.2.4", {"start": v(-71.84, -18.34) * mm, "end": v(-71.84, -33.58) * mm});
            skLineSegment(sketch, "E89.4.3.0", {"start": v(-69.3, -1.07) * mm, "end": v(-69.3, -16.3) * mm});
            skPoint(sketch, "E89.4.3.1", {"position": v(-70.57, -8.69) * mm});
            skLineSegment(sketch, "E89.4.3.2", {"start": v(-69.3, -16.3) * mm, "end": v(-71.84, -16.3) * mm});
            skLineSegment(sketch, "E89.4.3.3", {"start": v(-69.3, -1.07) * mm, "end": v(-71.84, -1.07) * mm});
            skLineSegment(sketch, "E89.4.3.4", {"start": v(-71.84, -1.07) * mm, "end": v(-71.84, -16.3) * mm});
            skLineSegment(sketch, "E89.4.4.0", {"start": v(-69.3, 16.2) * mm, "end": v(-69.3, 0.97) * mm});
            skPoint(sketch, "E89.4.4.1", {"position": v(-70.57, 8.59) * mm});
            skLineSegment(sketch, "E89.4.4.2", {"start": v(-69.3, 0.97) * mm, "end": v(-71.84, 0.97) * mm});
            skLineSegment(sketch, "E89.4.4.3", {"start": v(-69.3, 16.2) * mm, "end": v(-71.84, 16.2) * mm});
            skLineSegment(sketch, "E89.4.4.4", {"start": v(-71.84, 16.2) * mm, "end": v(-71.84, 0.97) * mm});
            skLineSegment(sketch, "E89.4.5.0", {"start": v(-69.3, 33.48) * mm, "end": v(-69.3, 18.24) * mm});
            skPoint(sketch, "E89.4.5.1", {"position": v(-70.57, 25.86) * mm});
            skLineSegment(sketch, "E89.4.5.2", {"start": v(-69.3, 18.24) * mm, "end": v(-71.84, 18.24) * mm});
            skLineSegment(sketch, "E89.4.5.3", {"start": v(-69.3, 33.48) * mm, "end": v(-71.84, 33.48) * mm});
            skLineSegment(sketch, "E89.4.5.4", {"start": v(-71.84, 33.48) * mm, "end": v(-71.84, 18.24) * mm});
            skLineSegment(sketch, "E89.4.6.0", {"start": v(-69.3, 50.75) * mm, "end": v(-69.3, 35.5) * mm});
            skPoint(sketch, "E89.4.6.1", {"position": v(-70.57, 43.13) * mm});
            skLineSegment(sketch, "E89.4.6.2", {"start": v(-69.3, 35.5) * mm, "end": v(-71.84, 35.5) * mm});
            skLineSegment(sketch, "E89.4.6.3", {"start": v(-69.3, 50.75) * mm, "end": v(-71.84, 50.75) * mm});
            skLineSegment(sketch, "E89.4.6.4", {"start": v(-71.84, 50.75) * mm, "end": v(-71.84, 35.5) * mm});
            skLineSegment(sketch, "E89.4.7.0", {"start": v(-69.3, 63.5) * mm, "end": v(-69.3, 52.78) * mm});
            skPoint(sketch, "E89.4.7.1", {"position": v(-70.57, 60.4) * mm});
            skLineSegment(sketch, "E89.4.7.2", {"start": v(-69.3, 52.78) * mm, "end": v(-71.84, 52.78) * mm});
            skLineSegment(sketch, "E89.4.7.4", {"start": v(-71.84, 63.5) * mm, "end": v(-71.84, 52.78) * mm});
            skLineSegment(sketch, "E89.5.0.0", {"start": v(-76.92, -52.88) * mm, "end": v(-76.92, -60.5) * mm});
            skPoint(sketch, "E89.5.0.1", {"position": v(-78.2, -60.5) * mm});
            skLineSegment(sketch, "E89.5.0.3", {"start": v(-76.92, -52.88) * mm, "end": v(-79.46, -52.88) * mm});
            skLineSegment(sketch, "E89.5.0.4", {"start": v(-79.46, -52.88) * mm, "end": v(-79.46, -60.5) * mm});
            skLineSegment(sketch, "E89.5.1.0", {"start": v(-76.92, -35.61) * mm, "end": v(-76.92, -50.85) * mm});
            skPoint(sketch, "E89.5.1.1", {"position": v(-78.2, -43.23) * mm});
            skLineSegment(sketch, "E89.5.1.2", {"start": v(-76.92, -50.85) * mm, "end": v(-79.46, -50.85) * mm});
            skLineSegment(sketch, "E89.5.1.3", {"start": v(-76.92, -35.61) * mm, "end": v(-79.46, -35.61) * mm});
            skLineSegment(sketch, "E89.5.1.4", {"start": v(-79.46, -35.61) * mm, "end": v(-79.46, -50.85) * mm});
            skLineSegment(sketch, "E89.5.2.0", {"start": v(-76.92, -18.34) * mm, "end": v(-76.92, -33.58) * mm});
            skPoint(sketch, "E89.5.2.1", {"position": v(-78.2, -25.96) * mm});
            skLineSegment(sketch, "E89.5.2.2", {"start": v(-76.92, -33.58) * mm, "end": v(-79.46, -33.58) * mm});
            skLineSegment(sketch, "E89.5.2.3", {"start": v(-76.92, -18.34) * mm, "end": v(-79.46, -18.34) * mm});
            skLineSegment(sketch, "E89.5.2.4", {"start": v(-79.46, -18.34) * mm, "end": v(-79.46, -33.58) * mm});
            skLineSegment(sketch, "E89.5.3.0", {"start": v(-76.92, -1.07) * mm, "end": v(-76.92, -16.3) * mm});
            skPoint(sketch, "E89.5.3.1", {"position": v(-78.2, -8.69) * mm});
            skLineSegment(sketch, "E89.5.3.2", {"start": v(-76.92, -16.3) * mm, "end": v(-79.46, -16.3) * mm});
            skLineSegment(sketch, "E89.5.3.3", {"start": v(-76.92, -1.07) * mm, "end": v(-79.46, -1.07) * mm});
            skLineSegment(sketch, "E89.5.3.4", {"start": v(-79.46, -1.07) * mm, "end": v(-79.46, -16.3) * mm});
            skLineSegment(sketch, "E89.5.4.0", {"start": v(-76.92, 16.2) * mm, "end": v(-76.92, 0.97) * mm});
            skPoint(sketch, "E89.5.4.1", {"position": v(-78.2, 8.59) * mm});
            skLineSegment(sketch, "E89.5.4.2", {"start": v(-76.92, 0.97) * mm, "end": v(-79.46, 0.97) * mm});
            skLineSegment(sketch, "E89.5.4.3", {"start": v(-76.92, 16.2) * mm, "end": v(-79.46, 16.2) * mm});
            skLineSegment(sketch, "E89.5.4.4", {"start": v(-79.46, 16.2) * mm, "end": v(-79.46, 0.97) * mm});
            skLineSegment(sketch, "E89.5.5.0", {"start": v(-76.92, 33.48) * mm, "end": v(-76.92, 18.24) * mm});
            skPoint(sketch, "E89.5.5.1", {"position": v(-78.2, 25.86) * mm});
            skLineSegment(sketch, "E89.5.5.2", {"start": v(-76.92, 18.24) * mm, "end": v(-79.46, 18.24) * mm});
            skLineSegment(sketch, "E89.5.5.3", {"start": v(-76.92, 33.48) * mm, "end": v(-79.46, 33.48) * mm});
            skLineSegment(sketch, "E89.5.5.4", {"start": v(-79.46, 33.48) * mm, "end": v(-79.46, 18.24) * mm});
            skLineSegment(sketch, "E89.5.6.0", {"start": v(-76.92, 50.75) * mm, "end": v(-76.92, 35.5) * mm});
            skPoint(sketch, "E89.5.6.1", {"position": v(-78.2, 43.13) * mm});
            skLineSegment(sketch, "E89.5.6.2", {"start": v(-76.92, 35.5) * mm, "end": v(-79.46, 35.5) * mm});
            skLineSegment(sketch, "E89.5.6.3", {"start": v(-76.92, 50.75) * mm, "end": v(-79.46, 50.75) * mm});
            skLineSegment(sketch, "E89.5.6.4", {"start": v(-79.46, 50.75) * mm, "end": v(-79.46, 35.5) * mm});
            skLineSegment(sketch, "E89.5.7.0", {"start": v(-76.92, 63.5) * mm, "end": v(-76.92, 52.78) * mm});
            skPoint(sketch, "E89.5.7.1", {"position": v(-78.2, 60.4) * mm});
            skLineSegment(sketch, "E89.5.7.2", {"start": v(-76.92, 52.78) * mm, "end": v(-79.46, 52.78) * mm});
            skLineSegment(sketch, "E89.5.7.4", {"start": v(-79.46, 63.5) * mm, "end": v(-79.46, 52.78) * mm});
            skLineSegment(sketch, "E90", {"start": v(-45.84, 65.15) * mm, "end": v(-42.03, 65.15) * mm, "construction": true});
            skLineSegment(sketch, "E91", {"start": v(-43.93, 65.15) * mm, "end": v(-43.93, 48.68) * mm, "construction": true});
            skLineSegment(sketch, "E92.bottom", {"start": v(-42.66, -44.17) * mm, "end": v(-45.2, -44.17) * mm});
            skLineSegment(sketch, "E92.top", {"start": v(-42.66, -59.41) * mm, "end": v(-45.2, -59.41) * mm});
            skLineSegment(sketch, "E92.left", {"start": v(-42.66, -44.17) * mm, "end": v(-42.66, -59.41) * mm});
            skLineSegment(sketch, "E92.right", {"start": v(-45.2, -44.17) * mm, "end": v(-45.2, -59.41) * mm});
            skPoint(sketch, "E92.middle", {"position": v(-43.93, -51.8) * mm});
            skLineSegment(sketch, "E93.0.1.0", {"start": v(-42.66, -26.4) * mm, "end": v(-42.66, -41.63) * mm});
            skLineSegment(sketch, "E93.0.1.1", {"start": v(-42.66, -41.63) * mm, "end": v(-45.2, -41.63) * mm});
            skPoint(sketch, "E93.0.1.2", {"position": v(-43.93, -34.01) * mm});
            skLineSegment(sketch, "E93.0.1.3", {"start": v(-42.66, -26.4) * mm, "end": v(-45.2, -26.4) * mm});
            skLineSegment(sketch, "E93.0.1.4", {"start": v(-45.2, -26.4) * mm, "end": v(-45.2, -41.63) * mm});
            skLineSegment(sketch, "E93.0.2.0", {"start": v(-42.66, -8.61) * mm, "end": v(-42.66, -23.85) * mm});
            skLineSegment(sketch, "E93.0.2.1", {"start": v(-42.66, -23.85) * mm, "end": v(-45.2, -23.85) * mm});
            skPoint(sketch, "E93.0.2.2", {"position": v(-43.93, -16.23) * mm});
            skLineSegment(sketch, "E93.0.2.3", {"start": v(-42.66, -8.61) * mm, "end": v(-45.2, -8.61) * mm});
            skLineSegment(sketch, "E93.0.2.4", {"start": v(-45.2, -8.61) * mm, "end": v(-45.2, -23.85) * mm});
            skLineSegment(sketch, "E93.0.3.0", {"start": v(-42.66, 9.17) * mm, "end": v(-42.66, -6.07) * mm});
            skLineSegment(sketch, "E93.0.3.1", {"start": v(-42.66, -6.07) * mm, "end": v(-45.2, -6.07) * mm});
            skPoint(sketch, "E93.0.3.2", {"position": v(-43.93, 1.55) * mm});
            skLineSegment(sketch, "E93.0.3.3", {"start": v(-42.66, 9.17) * mm, "end": v(-45.2, 9.17) * mm});
            skLineSegment(sketch, "E93.0.3.4", {"start": v(-45.2, 9.17) * mm, "end": v(-45.2, -6.07) * mm});
            skLineSegment(sketch, "E93.0.4.0", {"start": v(-42.66, 26.95) * mm, "end": v(-42.66, 11.7) * mm});
            skLineSegment(sketch, "E93.0.4.1", {"start": v(-42.66, 11.7) * mm, "end": v(-45.2, 11.7) * mm});
            skPoint(sketch, "E93.0.4.2", {"position": v(-43.93, 19.33) * mm});
            skLineSegment(sketch, "E93.0.4.3", {"start": v(-42.66, 26.95) * mm, "end": v(-45.2, 26.95) * mm});
            skLineSegment(sketch, "E93.0.4.4", {"start": v(-45.2, 26.95) * mm, "end": v(-45.2, 11.7) * mm});
            skLineSegment(sketch, "E93.0.5.0", {"start": v(-42.66, 44.73) * mm, "end": v(-42.66, 29.49) * mm});
            skLineSegment(sketch, "E93.0.5.1", {"start": v(-42.66, 29.49) * mm, "end": v(-45.2, 29.49) * mm});
            skPoint(sketch, "E93.0.5.2", {"position": v(-43.93, 37.1) * mm});
            skLineSegment(sketch, "E93.0.5.3", {"start": v(-42.66, 44.73) * mm, "end": v(-45.2, 44.73) * mm});
            skLineSegment(sketch, "E93.0.5.4", {"start": v(-45.2, 44.73) * mm, "end": v(-45.2, 29.49) * mm});
            skLineSegment(sketch, "E93.0.6.0", {"start": v(-42.66, 62.5) * mm, "end": v(-42.66, 47.27) * mm});
            skLineSegment(sketch, "E93.0.6.1", {"start": v(-42.66, 47.27) * mm, "end": v(-45.2, 47.27) * mm});
            skPoint(sketch, "E93.0.6.2", {"position": v(-43.93, 54.89) * mm});
            skLineSegment(sketch, "E93.0.6.3", {"start": v(-42.66, 62.5) * mm, "end": v(-45.2, 62.5) * mm});
            skLineSegment(sketch, "E93.0.6.4", {"start": v(-45.2, 62.5) * mm, "end": v(-45.2, 47.27) * mm});
            skLineSegment(sketch, "E93.1.0.0", {"start": v(-50.28, -44.17) * mm, "end": v(-50.28, -59.41) * mm});
            skLineSegment(sketch, "E93.1.0.1", {"start": v(-50.28, -59.41) * mm, "end": v(-52.82, -59.41) * mm});
            skPoint(sketch, "E93.1.0.2", {"position": v(-51.55, -51.8) * mm});
            skLineSegment(sketch, "E93.1.0.3", {"start": v(-50.28, -44.17) * mm, "end": v(-52.82, -44.17) * mm});
            skLineSegment(sketch, "E93.1.0.4", {"start": v(-52.82, -44.17) * mm, "end": v(-52.82, -59.41) * mm});
            skLineSegment(sketch, "E93.1.1.0", {"start": v(-50.28, -26.4) * mm, "end": v(-50.28, -41.63) * mm});
            skLineSegment(sketch, "E93.1.1.1", {"start": v(-50.28, -41.63) * mm, "end": v(-52.82, -41.63) * mm});
            skPoint(sketch, "E93.1.1.2", {"position": v(-51.55, -34.01) * mm});
            skLineSegment(sketch, "E93.1.1.3", {"start": v(-50.28, -26.4) * mm, "end": v(-52.82, -26.4) * mm});
            skLineSegment(sketch, "E93.1.1.4", {"start": v(-52.82, -26.4) * mm, "end": v(-52.82, -41.63) * mm});
            skLineSegment(sketch, "E93.1.2.0", {"start": v(-50.28, -8.61) * mm, "end": v(-50.28, -23.85) * mm});
            skLineSegment(sketch, "E93.1.2.1", {"start": v(-50.28, -23.85) * mm, "end": v(-52.82, -23.85) * mm});
            skPoint(sketch, "E93.1.2.2", {"position": v(-51.55, -16.23) * mm});
            skLineSegment(sketch, "E93.1.2.3", {"start": v(-50.28, -8.61) * mm, "end": v(-52.82, -8.61) * mm});
            skLineSegment(sketch, "E93.1.2.4", {"start": v(-52.82, -8.61) * mm, "end": v(-52.82, -23.85) * mm});
            skLineSegment(sketch, "E93.1.3.0", {"start": v(-50.28, 9.17) * mm, "end": v(-50.28, -6.07) * mm});
            skLineSegment(sketch, "E93.1.3.1", {"start": v(-50.28, -6.07) * mm, "end": v(-52.82, -6.07) * mm});
            skPoint(sketch, "E93.1.3.2", {"position": v(-51.55, 1.55) * mm});
            skLineSegment(sketch, "E93.1.3.3", {"start": v(-50.28, 9.17) * mm, "end": v(-52.82, 9.17) * mm});
            skLineSegment(sketch, "E93.1.3.4", {"start": v(-52.82, 9.17) * mm, "end": v(-52.82, -6.07) * mm});
            skLineSegment(sketch, "E93.1.4.0", {"start": v(-50.28, 26.95) * mm, "end": v(-50.28, 11.7) * mm});
            skLineSegment(sketch, "E93.1.4.1", {"start": v(-50.28, 11.7) * mm, "end": v(-52.82, 11.7) * mm});
            skPoint(sketch, "E93.1.4.2", {"position": v(-51.55, 19.33) * mm});
            skLineSegment(sketch, "E93.1.4.3", {"start": v(-50.28, 26.95) * mm, "end": v(-52.82, 26.95) * mm});
            skLineSegment(sketch, "E93.1.4.4", {"start": v(-52.82, 26.95) * mm, "end": v(-52.82, 11.7) * mm});
            skLineSegment(sketch, "E93.1.5.0", {"start": v(-50.28, 44.73) * mm, "end": v(-50.28, 29.49) * mm});
            skLineSegment(sketch, "E93.1.5.1", {"start": v(-50.28, 29.49) * mm, "end": v(-52.82, 29.49) * mm});
            skPoint(sketch, "E93.1.5.2", {"position": v(-51.55, 37.1) * mm});
            skLineSegment(sketch, "E93.1.5.3", {"start": v(-50.28, 44.73) * mm, "end": v(-52.82, 44.73) * mm});
            skLineSegment(sketch, "E93.1.5.4", {"start": v(-52.82, 44.73) * mm, "end": v(-52.82, 29.49) * mm});
            skLineSegment(sketch, "E93.1.6.0", {"start": v(-50.28, 62.5) * mm, "end": v(-50.28, 47.27) * mm});
            skLineSegment(sketch, "E93.1.6.1", {"start": v(-50.28, 47.27) * mm, "end": v(-52.82, 47.27) * mm});
            skPoint(sketch, "E93.1.6.2", {"position": v(-51.55, 54.89) * mm});
            skLineSegment(sketch, "E93.1.6.3", {"start": v(-50.28, 62.5) * mm, "end": v(-52.82, 62.5) * mm});
            skLineSegment(sketch, "E93.1.6.4", {"start": v(-52.82, 62.5) * mm, "end": v(-52.82, 47.27) * mm});
            skLineSegment(sketch, "E93.2.0.0", {"start": v(-57.9, -44.17) * mm, "end": v(-57.9, -59.41) * mm});
            skLineSegment(sketch, "E93.2.0.1", {"start": v(-57.9, -59.41) * mm, "end": v(-60.44, -59.41) * mm});
            skPoint(sketch, "E93.2.0.2", {"position": v(-59.17, -51.8) * mm});
            skLineSegment(sketch, "E93.2.0.3", {"start": v(-57.9, -44.17) * mm, "end": v(-60.44, -44.17) * mm});
            skLineSegment(sketch, "E93.2.0.4", {"start": v(-60.44, -44.17) * mm, "end": v(-60.44, -59.41) * mm});
            skLineSegment(sketch, "E93.2.1.0", {"start": v(-57.9, -26.4) * mm, "end": v(-57.9, -41.63) * mm});
            skLineSegment(sketch, "E93.2.1.1", {"start": v(-57.9, -41.63) * mm, "end": v(-60.44, -41.63) * mm});
            skPoint(sketch, "E93.2.1.2", {"position": v(-59.17, -34.01) * mm});
            skLineSegment(sketch, "E93.2.1.3", {"start": v(-57.9, -26.4) * mm, "end": v(-60.44, -26.4) * mm});
            skLineSegment(sketch, "E93.2.1.4", {"start": v(-60.44, -26.4) * mm, "end": v(-60.44, -41.63) * mm});
            skLineSegment(sketch, "E93.2.2.0", {"start": v(-57.9, -8.61) * mm, "end": v(-57.9, -23.85) * mm});
            skLineSegment(sketch, "E93.2.2.1", {"start": v(-57.9, -23.85) * mm, "end": v(-60.44, -23.85) * mm});
            skPoint(sketch, "E93.2.2.2", {"position": v(-59.17, -16.23) * mm});
            skLineSegment(sketch, "E93.2.2.3", {"start": v(-57.9, -8.61) * mm, "end": v(-60.44, -8.61) * mm});
            skLineSegment(sketch, "E93.2.2.4", {"start": v(-60.44, -8.61) * mm, "end": v(-60.44, -23.85) * mm});
            skLineSegment(sketch, "E93.2.3.0", {"start": v(-57.9, 9.17) * mm, "end": v(-57.9, -6.07) * mm});
            skLineSegment(sketch, "E93.2.3.1", {"start": v(-57.9, -6.07) * mm, "end": v(-60.44, -6.07) * mm});
            skPoint(sketch, "E93.2.3.2", {"position": v(-59.17, 1.55) * mm});
            skLineSegment(sketch, "E93.2.3.3", {"start": v(-57.9, 9.17) * mm, "end": v(-60.44, 9.17) * mm});
            skLineSegment(sketch, "E93.2.3.4", {"start": v(-60.44, 9.17) * mm, "end": v(-60.44, -6.07) * mm});
            skLineSegment(sketch, "E93.2.4.0", {"start": v(-57.9, 26.95) * mm, "end": v(-57.9, 11.7) * mm});
            skLineSegment(sketch, "E93.2.4.1", {"start": v(-57.9, 11.7) * mm, "end": v(-60.44, 11.7) * mm});
            skPoint(sketch, "E93.2.4.2", {"position": v(-59.17, 19.33) * mm});
            skLineSegment(sketch, "E93.2.4.3", {"start": v(-57.9, 26.95) * mm, "end": v(-60.44, 26.95) * mm});
            skLineSegment(sketch, "E93.2.4.4", {"start": v(-60.44, 26.95) * mm, "end": v(-60.44, 11.7) * mm});
            skLineSegment(sketch, "E93.2.5.0", {"start": v(-57.9, 44.73) * mm, "end": v(-57.9, 29.49) * mm});
            skLineSegment(sketch, "E93.2.5.1", {"start": v(-57.9, 29.49) * mm, "end": v(-60.44, 29.49) * mm});
            skPoint(sketch, "E93.2.5.2", {"position": v(-59.17, 37.1) * mm});
            skLineSegment(sketch, "E93.2.5.3", {"start": v(-57.9, 44.73) * mm, "end": v(-60.44, 44.73) * mm});
            skLineSegment(sketch, "E93.2.5.4", {"start": v(-60.44, 44.73) * mm, "end": v(-60.44, 29.49) * mm});
            skLineSegment(sketch, "E93.2.6.0", {"start": v(-57.9, 62.5) * mm, "end": v(-57.9, 47.27) * mm});
            skLineSegment(sketch, "E93.2.6.1", {"start": v(-57.9, 47.27) * mm, "end": v(-60.44, 47.27) * mm});
            skPoint(sketch, "E93.2.6.2", {"position": v(-59.17, 54.89) * mm});
            skLineSegment(sketch, "E93.2.6.3", {"start": v(-57.9, 62.5) * mm, "end": v(-60.44, 62.5) * mm});
            skLineSegment(sketch, "E93.2.6.4", {"start": v(-60.44, 62.5) * mm, "end": v(-60.44, 47.27) * mm});
            skLineSegment(sketch, "E93.3.0.0", {"start": v(-65.52, -44.17) * mm, "end": v(-65.52, -59.41) * mm});
            skLineSegment(sketch, "E93.3.0.1", {"start": v(-65.52, -59.41) * mm, "end": v(-68.06, -59.41) * mm});
            skPoint(sketch, "E93.3.0.2", {"position": v(-66.8, -51.8) * mm});
            skLineSegment(sketch, "E93.3.0.3", {"start": v(-65.52, -44.17) * mm, "end": v(-68.06, -44.17) * mm});
            skLineSegment(sketch, "E93.3.0.4", {"start": v(-68.06, -44.17) * mm, "end": v(-68.06, -59.41) * mm});
            skLineSegment(sketch, "E93.3.1.0", {"start": v(-65.52, -26.4) * mm, "end": v(-65.52, -41.63) * mm});
            skLineSegment(sketch, "E93.3.1.1", {"start": v(-65.52, -41.63) * mm, "end": v(-68.06, -41.63) * mm});
            skPoint(sketch, "E93.3.1.2", {"position": v(-66.8, -34.01) * mm});
            skLineSegment(sketch, "E93.3.1.3", {"start": v(-65.52, -26.4) * mm, "end": v(-68.06, -26.4) * mm});
            skLineSegment(sketch, "E93.3.1.4", {"start": v(-68.06, -26.4) * mm, "end": v(-68.06, -41.63) * mm});
            skLineSegment(sketch, "E93.3.2.0", {"start": v(-65.52, -8.61) * mm, "end": v(-65.52, -23.85) * mm});
            skLineSegment(sketch, "E93.3.2.1", {"start": v(-65.52, -23.85) * mm, "end": v(-68.06, -23.85) * mm});
            skPoint(sketch, "E93.3.2.2", {"position": v(-66.8, -16.23) * mm});
            skLineSegment(sketch, "E93.3.2.3", {"start": v(-65.52, -8.61) * mm, "end": v(-68.06, -8.61) * mm});
            skLineSegment(sketch, "E93.3.2.4", {"start": v(-68.06, -8.61) * mm, "end": v(-68.06, -23.85) * mm});
            skLineSegment(sketch, "E93.3.3.0", {"start": v(-65.52, 9.17) * mm, "end": v(-65.52, -6.07) * mm});
            skLineSegment(sketch, "E93.3.3.1", {"start": v(-65.52, -6.07) * mm, "end": v(-68.06, -6.07) * mm});
            skPoint(sketch, "E93.3.3.2", {"position": v(-66.8, 1.55) * mm});
            skLineSegment(sketch, "E93.3.3.3", {"start": v(-65.52, 9.17) * mm, "end": v(-68.06, 9.17) * mm});
            skLineSegment(sketch, "E93.3.3.4", {"start": v(-68.06, 9.17) * mm, "end": v(-68.06, -6.07) * mm});
            skLineSegment(sketch, "E93.3.4.0", {"start": v(-65.52, 26.95) * mm, "end": v(-65.52, 11.7) * mm});
            skLineSegment(sketch, "E93.3.4.1", {"start": v(-65.52, 11.7) * mm, "end": v(-68.06, 11.7) * mm});
            skPoint(sketch, "E93.3.4.2", {"position": v(-66.8, 19.33) * mm});
            skLineSegment(sketch, "E93.3.4.3", {"start": v(-65.52, 26.95) * mm, "end": v(-68.06, 26.95) * mm});
            skLineSegment(sketch, "E93.3.4.4", {"start": v(-68.06, 26.95) * mm, "end": v(-68.06, 11.7) * mm});
            skLineSegment(sketch, "E93.3.5.0", {"start": v(-65.52, 44.73) * mm, "end": v(-65.52, 29.49) * mm});
            skLineSegment(sketch, "E93.3.5.1", {"start": v(-65.52, 29.49) * mm, "end": v(-68.06, 29.49) * mm});
            skPoint(sketch, "E93.3.5.2", {"position": v(-66.8, 37.1) * mm});
            skLineSegment(sketch, "E93.3.5.3", {"start": v(-65.52, 44.73) * mm, "end": v(-68.06, 44.73) * mm});
            skLineSegment(sketch, "E93.3.5.4", {"start": v(-68.06, 44.73) * mm, "end": v(-68.06, 29.49) * mm});
            skLineSegment(sketch, "E93.3.6.0", {"start": v(-65.52, 62.5) * mm, "end": v(-65.52, 47.27) * mm});
            skLineSegment(sketch, "E93.3.6.1", {"start": v(-65.52, 47.27) * mm, "end": v(-68.06, 47.27) * mm});
            skPoint(sketch, "E93.3.6.2", {"position": v(-66.8, 54.89) * mm});
            skLineSegment(sketch, "E93.3.6.3", {"start": v(-65.52, 62.5) * mm, "end": v(-68.06, 62.5) * mm});
            skLineSegment(sketch, "E93.3.6.4", {"start": v(-68.06, 62.5) * mm, "end": v(-68.06, 47.27) * mm});
            skLineSegment(sketch, "E93.4.0.0", {"start": v(-73.14, -44.17) * mm, "end": v(-73.14, -59.41) * mm});
            skLineSegment(sketch, "E93.4.0.1", {"start": v(-73.14, -59.41) * mm, "end": v(-75.68, -59.41) * mm});
            skPoint(sketch, "E93.4.0.2", {"position": v(-74.41, -51.8) * mm});
            skLineSegment(sketch, "E93.4.0.3", {"start": v(-73.14, -44.17) * mm, "end": v(-75.68, -44.17) * mm});
            skLineSegment(sketch, "E93.4.0.4", {"start": v(-75.68, -44.17) * mm, "end": v(-75.68, -59.41) * mm});
            skLineSegment(sketch, "E93.4.1.0", {"start": v(-73.14, -26.4) * mm, "end": v(-73.14, -41.63) * mm});
            skLineSegment(sketch, "E93.4.1.1", {"start": v(-73.14, -41.63) * mm, "end": v(-75.68, -41.63) * mm});
            skPoint(sketch, "E93.4.1.2", {"position": v(-74.41, -34.01) * mm});
            skLineSegment(sketch, "E93.4.1.3", {"start": v(-73.14, -26.4) * mm, "end": v(-75.68, -26.4) * mm});
            skLineSegment(sketch, "E93.4.1.4", {"start": v(-75.68, -26.4) * mm, "end": v(-75.68, -41.63) * mm});
            skLineSegment(sketch, "E93.4.2.0", {"start": v(-73.14, -8.61) * mm, "end": v(-73.14, -23.85) * mm});
            skLineSegment(sketch, "E93.4.2.1", {"start": v(-73.14, -23.85) * mm, "end": v(-75.68, -23.85) * mm});
            skPoint(sketch, "E93.4.2.2", {"position": v(-74.41, -16.23) * mm});
            skLineSegment(sketch, "E93.4.2.3", {"start": v(-73.14, -8.61) * mm, "end": v(-75.68, -8.61) * mm});
            skLineSegment(sketch, "E93.4.2.4", {"start": v(-75.68, -8.61) * mm, "end": v(-75.68, -23.85) * mm});
            skLineSegment(sketch, "E93.4.3.0", {"start": v(-73.14, 9.17) * mm, "end": v(-73.14, -6.07) * mm});
            skLineSegment(sketch, "E93.4.3.1", {"start": v(-73.14, -6.07) * mm, "end": v(-75.68, -6.07) * mm});
            skPoint(sketch, "E93.4.3.2", {"position": v(-74.41, 1.55) * mm});
            skLineSegment(sketch, "E93.4.3.3", {"start": v(-73.14, 9.17) * mm, "end": v(-75.68, 9.17) * mm});
            skLineSegment(sketch, "E93.4.3.4", {"start": v(-75.68, 9.17) * mm, "end": v(-75.68, -6.07) * mm});
            skLineSegment(sketch, "E93.4.4.0", {"start": v(-73.14, 26.95) * mm, "end": v(-73.14, 11.7) * mm});
            skLineSegment(sketch, "E93.4.4.1", {"start": v(-73.14, 11.7) * mm, "end": v(-75.68, 11.7) * mm});
            skPoint(sketch, "E93.4.4.2", {"position": v(-74.41, 19.33) * mm});
            skLineSegment(sketch, "E93.4.4.3", {"start": v(-73.14, 26.95) * mm, "end": v(-75.68, 26.95) * mm});
            skLineSegment(sketch, "E93.4.4.4", {"start": v(-75.68, 26.95) * mm, "end": v(-75.68, 11.7) * mm});
            skLineSegment(sketch, "E93.4.5.0", {"start": v(-73.14, 44.73) * mm, "end": v(-73.14, 29.49) * mm});
            skLineSegment(sketch, "E93.4.5.1", {"start": v(-73.14, 29.49) * mm, "end": v(-75.68, 29.49) * mm});
            skPoint(sketch, "E93.4.5.2", {"position": v(-74.41, 37.1) * mm});
            skLineSegment(sketch, "E93.4.5.3", {"start": v(-73.14, 44.73) * mm, "end": v(-75.68, 44.73) * mm});
            skLineSegment(sketch, "E93.4.5.4", {"start": v(-75.68, 44.73) * mm, "end": v(-75.68, 29.49) * mm});
            skLineSegment(sketch, "E93.4.6.0", {"start": v(-73.14, 62.5) * mm, "end": v(-73.14, 47.27) * mm});
            skLineSegment(sketch, "E93.4.6.1", {"start": v(-73.14, 47.27) * mm, "end": v(-75.68, 47.27) * mm});
            skPoint(sketch, "E93.4.6.2", {"position": v(-74.41, 54.89) * mm});
            skLineSegment(sketch, "E93.4.6.3", {"start": v(-73.14, 62.5) * mm, "end": v(-75.68, 62.5) * mm});
            skLineSegment(sketch, "E93.4.6.4", {"start": v(-75.68, 62.5) * mm, "end": v(-75.68, 47.27) * mm});
            skLineSegment(sketch, "E93.direction1", {"start": v(-45.2, -59.41) * mm, "end": v(-52.82, -59.41) * mm, "construction": true});
            skLineSegment(sketch, "E93.direction2", {"start": v(-45.2, -59.41) * mm, "end": v(-45.2, -41.63) * mm, "construction": true});
            skLineSegment(sketch, "E94", {"start": v(-41.36, -60.5) * mm, "end": v(-38.82, -60.5) * mm});
            skLineSegment(sketch, "E95", {"start": v(-79.46, -60.5) * mm, "end": v(-76.92, -60.5) * mm});
            skLineSegment(sketch, "E96", {"start": v(-71.84, -60.5) * mm, "end": v(-69.3, -60.5) * mm});
            skLineSegment(sketch, "E97", {"start": v(-64.22, -60.5) * mm, "end": v(-61.68, -60.5) * mm});
            skLineSegment(sketch, "E98", {"start": v(-56.6, -60.5) * mm, "end": v(-54.06, -60.5) * mm});
            skLineSegment(sketch, "E99", {"start": v(-48.98, -60.5) * mm, "end": v(-46.44, -60.5) * mm});
            skPoint(sketch, "E89.4.0.2.end.orphan", {"position": v(-71.84, -68.12) * mm});
            skPoint(sketch, "E89.4.0.2.start.orphan", {"position": v(-69.3, -68.12) * mm});
            skPoint(sketch, "E89.3.0.2.end.orphan", {"position": v(-64.22, -68.12) * mm});
            skPoint(sketch, "E89.3.0.2.start.orphan", {"position": v(-61.68, -68.12) * mm});
            skPoint(sketch, "E89.2.0.2.end.orphan", {"position": v(-56.6, -68.12) * mm});
            skPoint(sketch, "E89.2.0.2.start.orphan", {"position": v(-54.06, -68.12) * mm});
            skLineSegment(sketch, "E100.trimOffspring", {"start": v(-41.36, -60.5) * mm, "end": v(-41.36, -50.85) * mm, "construction": true});
            skPoint(sketch, "E88.top.start.orphan", {"position": v(-38.82, -68.12) * mm});
            skPoint(sketch, "E101.trimOffspring.end.orphan", {"position": v(-41.36, -68.12) * mm});
            skPoint(sketch, "E89.1.0.2.end.orphan", {"position": v(-48.98, -68.12) * mm});
            skPoint(sketch, "E89.1.0.2.start.orphan", {"position": v(-46.44, -68.12) * mm});
            skLineSegment(sketch, "E102", {"start": v(-79.46, 63.5) * mm, "end": v(-76.92, 63.5) * mm});
            skLineSegment(sketch, "E103", {"start": v(-71.84, 63.5) * mm, "end": v(-69.3, 63.5) * mm});
            skLineSegment(sketch, "E104", {"start": v(-48.98, 63.5) * mm, "end": v(-46.44, 63.5) * mm});
            skLineSegment(sketch, "E105", {"start": v(-64.22, 63.5) * mm, "end": v(-61.68, 63.5) * mm});
            skLineSegment(sketch, "E106", {"start": v(-56.6, 63.5) * mm, "end": v(-54.06, 63.5) * mm});
            skLineSegment(sketch, "E107", {"start": v(-41.36, 63.5) * mm, "end": v(-38.82, 63.5) * mm});
            skLineSegment(sketch, "E108.MirrorCS", {"start": v(42.66, -59.41) * mm, "end": v(45.2, -59.41) * mm});
            skLineSegment(sketch, "E109.MirrorCS", {"start": v(65.52, 62.5) * mm, "end": v(68.06, 62.5) * mm});
            skLineSegment(sketch, "E110.MirrorCS", {"start": v(45.2, -59.41) * mm, "end": v(52.82, -59.41) * mm, "construction": true});
            skLineSegment(sketch, "E111.MirrorCS", {"start": v(50.28, -59.41) * mm, "end": v(52.82, -59.41) * mm});
            skLineSegment(sketch, "E112.MirrorCS", {"start": v(56.6, 63.5) * mm, "end": v(54.06, 63.5) * mm});
            skLineSegment(sketch, "E113.MirrorCS", {"start": v(64.22, -60.5) * mm, "end": v(61.68, -60.5) * mm});
            skLineSegment(sketch, "E114.MirrorCS", {"start": v(38.82, -50.85) * mm, "end": v(41.36, -50.85) * mm});
            skLineSegment(sketch, "E115.MirrorCS", {"start": v(48.98, 63.5) * mm, "end": v(46.44, 63.5) * mm});
            skLineSegment(sketch, "E116.MirrorCS", {"start": v(42.66, 62.5) * mm, "end": v(45.2, 62.5) * mm});
            skLineSegment(sketch, "E117.MirrorCS", {"start": v(64.22, 63.5) * mm, "end": v(61.68, 63.5) * mm});
            skLineSegment(sketch, "E118.MirrorCS", {"start": v(48.98, -60.5) * mm, "end": v(46.44, -60.5) * mm});
            skLineSegment(sketch, "E119.MirrorCS", {"start": v(57.9, 62.5) * mm, "end": v(60.44, 62.5) * mm});
            skLineSegment(sketch, "E120.MirrorCS", {"start": v(38.82, -52.88) * mm, "end": v(41.36, -52.88) * mm});
            skLineSegment(sketch, "E121.MirrorCS", {"start": v(73.14, 29.49) * mm, "end": v(75.68, 29.49) * mm});
            skLineSegment(sketch, "E122.MirrorCS", {"start": v(65.52, 11.7) * mm, "end": v(68.06, 11.7) * mm});
            skLineSegment(sketch, "E123.MirrorCS", {"start": v(73.14, -41.63) * mm, "end": v(75.68, -41.63) * mm});
            skLineSegment(sketch, "E124.MirrorCS", {"start": v(42.66, -41.63) * mm, "end": v(45.2, -41.63) * mm});
            skLineSegment(sketch, "E125.MirrorCS", {"start": v(54.06, 52.78) * mm, "end": v(56.6, 52.78) * mm});
            skLineSegment(sketch, "E126.MirrorCS", {"start": v(69.3, -1.07) * mm, "end": v(71.84, -1.07) * mm});
            skLineSegment(sketch, "E127.MirrorCS", {"start": v(46.44, 0.97) * mm, "end": v(48.98, 0.97) * mm});
            skLineSegment(sketch, "E128.MirrorCS", {"start": v(57.9, -23.85) * mm, "end": v(60.44, -23.85) * mm});
            skLineSegment(sketch, "E129.MirrorCS", {"start": v(46.44, 16.2) * mm, "end": v(48.98, 16.2) * mm});
            skLineSegment(sketch, "E130.MirrorCS", {"start": v(65.52, 9.17) * mm, "end": v(68.06, 9.17) * mm});
            skLineSegment(sketch, "E131.MirrorCS", {"start": v(50.28, -41.63) * mm, "end": v(52.82, -41.63) * mm});
            skLineSegment(sketch, "E132.MirrorCS", {"start": v(50.28, -44.17) * mm, "end": v(52.82, -44.17) * mm});
            skLineSegment(sketch, "E133.MirrorCS", {"start": v(38.82, 0.97) * mm, "end": v(41.36, 0.97) * mm});
            skLineSegment(sketch, "E134.MirrorCS", {"start": v(50.28, -23.85) * mm, "end": v(52.82, -23.85) * mm});
            skLineSegment(sketch, "E135.MirrorCS", {"start": v(46.44, -35.61) * mm, "end": v(48.98, -35.61) * mm});
            skLineSegment(sketch, "E136.MirrorCS", {"start": v(50.28, 26.95) * mm, "end": v(52.82, 26.95) * mm});
            skLineSegment(sketch, "E137.MirrorCS", {"start": v(76.92, -35.61) * mm, "end": v(79.46, -35.61) * mm});
            skLineSegment(sketch, "E138.MirrorCS", {"start": v(76.92, 0.97) * mm, "end": v(79.46, 0.97) * mm});
            skLineSegment(sketch, "E139.MirrorCS", {"start": v(76.92, 33.48) * mm, "end": v(79.46, 33.48) * mm});
            skLineSegment(sketch, "E140.MirrorCS", {"start": v(38.82, -18.34) * mm, "end": v(41.36, -18.34) * mm});
            skLineSegment(sketch, "E141.MirrorCS", {"start": v(38.82, 18.24) * mm, "end": v(41.36, 18.24) * mm});
            skLineSegment(sketch, "E142.MirrorCS", {"start": v(57.9, -44.17) * mm, "end": v(60.44, -44.17) * mm});
            skLineSegment(sketch, "E143.MirrorCS", {"start": v(42.66, 9.17) * mm, "end": v(45.2, 9.17) * mm});
            skLineSegment(sketch, "E144.MirrorCS", {"start": v(57.9, 44.73) * mm, "end": v(60.44, 44.73) * mm});
            skLineSegment(sketch, "E145.MirrorCS", {"start": v(54.06, -35.61) * mm, "end": v(56.6, -35.61) * mm});
            skLineSegment(sketch, "E146.MirrorCS", {"start": v(46.44, -18.34) * mm, "end": v(48.98, -18.34) * mm});
            skLineSegment(sketch, "E147.MirrorCS", {"start": v(69.3, -35.61) * mm, "end": v(71.84, -35.61) * mm});
            skLineSegment(sketch, "E148.MirrorCS", {"start": v(57.9, -41.63) * mm, "end": v(60.44, -41.63) * mm});
            skLineSegment(sketch, "E149.MirrorCS", {"start": v(73.14, 9.17) * mm, "end": v(75.68, 9.17) * mm});
            skLineSegment(sketch, "E150.MirrorCS", {"start": v(57.9, 47.27) * mm, "end": v(60.44, 47.27) * mm});
            skLineSegment(sketch, "E151.MirrorCS", {"start": v(50.28, 29.49) * mm, "end": v(52.82, 29.49) * mm});
            skLineSegment(sketch, "E152.MirrorCS", {"start": v(61.68, -52.88) * mm, "end": v(64.22, -52.88) * mm});
            skLineSegment(sketch, "E153.MirrorCS", {"start": v(42.66, -23.85) * mm, "end": v(45.2, -23.85) * mm});
            skLineSegment(sketch, "E154.MirrorCS", {"start": v(46.44, 18.24) * mm, "end": v(48.98, 18.24) * mm});
            skLineSegment(sketch, "E155.MirrorCS", {"start": v(69.3, -18.34) * mm, "end": v(71.84, -18.34) * mm});
            skLineSegment(sketch, "E156.MirrorCS", {"start": v(50.28, 9.17) * mm, "end": v(52.82, 9.17) * mm});
            skLineSegment(sketch, "E157.MirrorCS", {"start": v(46.44, -16.3) * mm, "end": v(48.98, -16.3) * mm});
            skLineSegment(sketch, "E158.MirrorCS", {"start": v(41.36, -60.5) * mm, "end": v(38.82, -60.5) * mm});
            skLineSegment(sketch, "E159.MirrorCS", {"start": v(69.3, -50.85) * mm, "end": v(71.84, -50.85) * mm});
            skLineSegment(sketch, "E160.MirrorCS", {"start": v(69.3, 18.24) * mm, "end": v(71.84, 18.24) * mm});
            skLineSegment(sketch, "E161.MirrorCS", {"start": v(50.28, -26.4) * mm, "end": v(52.82, -26.4) * mm});
            skLineSegment(sketch, "E162.MirrorCS", {"start": v(76.92, -50.85) * mm, "end": v(79.46, -50.85) * mm});
            skLineSegment(sketch, "E163.MirrorCS", {"start": v(69.3, -33.58) * mm, "end": v(71.84, -33.58) * mm});
            skLineSegment(sketch, "E164.MirrorCS", {"start": v(76.92, 35.5) * mm, "end": v(79.46, 35.5) * mm});
            skLineSegment(sketch, "E165.MirrorCS", {"start": v(57.9, -59.41) * mm, "end": v(60.44, -59.41) * mm});
            skLineSegment(sketch, "E166.MirrorCS", {"start": v(42.66, 11.7) * mm, "end": v(45.2, 11.7) * mm});
            skLineSegment(sketch, "E167.MirrorCS", {"start": v(76.92, -52.88) * mm, "end": v(79.46, -52.88) * mm});
            skLineSegment(sketch, "E168.MirrorCS", {"start": v(61.68, 50.75) * mm, "end": v(64.22, 50.75) * mm});
            skLineSegment(sketch, "E169.MirrorCS", {"start": v(46.44, 35.5) * mm, "end": v(48.98, 35.5) * mm});
            skLineSegment(sketch, "E170.MirrorCS", {"start": v(65.52, -59.41) * mm, "end": v(68.06, -59.41) * mm});
            skLineSegment(sketch, "E171.MirrorCS", {"start": v(69.3, 50.75) * mm, "end": v(71.84, 50.75) * mm});
            skLineSegment(sketch, "E172.MirrorCS", {"start": v(54.06, 33.48) * mm, "end": v(56.6, 33.48) * mm});
            skLineSegment(sketch, "E173.MirrorCS", {"start": v(73.14, -44.17) * mm, "end": v(75.68, -44.17) * mm});
            skLineSegment(sketch, "E174.MirrorCS", {"start": v(69.3, 52.78) * mm, "end": v(71.84, 52.78) * mm});
            skLineSegment(sketch, "E175.MirrorCS", {"start": v(38.82, -16.3) * mm, "end": v(41.36, -16.3) * mm});
            skLineSegment(sketch, "E176.MirrorCS", {"start": v(61.68, 52.78) * mm, "end": v(64.22, 52.78) * mm});
            skLineSegment(sketch, "E177.MirrorCS", {"start": v(54.06, -16.3) * mm, "end": v(56.6, -16.3) * mm});
            skLineSegment(sketch, "E178.MirrorCS", {"start": v(38.82, 16.2) * mm, "end": v(41.36, 16.2) * mm});
            skLineSegment(sketch, "E179.MirrorCS", {"start": v(69.3, 33.48) * mm, "end": v(71.84, 33.48) * mm});
            skLineSegment(sketch, "E180.MirrorCS", {"start": v(50.28, -6.07) * mm, "end": v(52.82, -6.07) * mm});
            skLineSegment(sketch, "E181.MirrorCS", {"start": v(42.66, 47.27) * mm, "end": v(45.2, 47.27) * mm});
            skLineSegment(sketch, "E182.MirrorCS", {"start": v(38.82, 52.78) * mm, "end": v(41.36, 52.78) * mm});
            skLineSegment(sketch, "E183.MirrorCS", {"start": v(54.06, -1.07) * mm, "end": v(56.6, -1.07) * mm});
            skLineSegment(sketch, "E184.MirrorCS", {"start": v(79.46, 63.5) * mm, "end": v(76.92, 63.5) * mm});
            skLineSegment(sketch, "E185.MirrorCS", {"start": v(69.3, 35.5) * mm, "end": v(71.84, 35.5) * mm});
            skLineSegment(sketch, "E186.MirrorCS", {"start": v(50.28, 44.73) * mm, "end": v(52.82, 44.73) * mm});
            skLineSegment(sketch, "E187.MirrorCS", {"start": v(50.28, 11.7) * mm, "end": v(52.82, 11.7) * mm});
            skLineSegment(sketch, "E188.MirrorCS", {"start": v(61.68, 0.97) * mm, "end": v(64.22, 0.97) * mm});
            skLineSegment(sketch, "E189.MirrorCS", {"start": v(71.84, -60.5) * mm, "end": v(69.3, -60.5) * mm});
            skLineSegment(sketch, "E190.MirrorCS", {"start": v(38.82, -33.58) * mm, "end": v(41.36, -33.58) * mm});
            skLineSegment(sketch, "E191.MirrorCS", {"start": v(73.14, 44.73) * mm, "end": v(75.68, 44.73) * mm});
            skLineSegment(sketch, "E192.MirrorCS", {"start": v(76.92, -16.3) * mm, "end": v(79.46, -16.3) * mm});
            skLineSegment(sketch, "E193.MirrorCS", {"start": v(61.68, -1.07) * mm, "end": v(64.22, -1.07) * mm});
            skLineSegment(sketch, "E194.MirrorCS", {"start": v(76.92, 18.24) * mm, "end": v(79.46, 18.24) * mm});
            skLineSegment(sketch, "E195.MirrorCS", {"start": v(57.9, 11.7) * mm, "end": v(60.44, 11.7) * mm});
            skLineSegment(sketch, "E196.MirrorCS", {"start": v(65.52, 26.95) * mm, "end": v(68.06, 26.95) * mm});
            skLineSegment(sketch, "E197.MirrorCS", {"start": v(61.68, -18.34) * mm, "end": v(64.22, -18.34) * mm});
            skLineSegment(sketch, "E198.MirrorCS", {"start": v(73.14, -23.85) * mm, "end": v(75.68, -23.85) * mm});
            skLineSegment(sketch, "E199.MirrorCS", {"start": v(42.66, -44.17) * mm, "end": v(45.2, -44.17) * mm});
            skLineSegment(sketch, "E200.MirrorCS", {"start": v(50.28, 47.27) * mm, "end": v(52.82, 47.27) * mm});
            skLineSegment(sketch, "E201.MirrorCS", {"start": v(65.52, -23.85) * mm, "end": v(68.06, -23.85) * mm});
            skLineSegment(sketch, "E202.MirrorCS", {"start": v(65.52, -44.17) * mm, "end": v(68.06, -44.17) * mm});
            skLineSegment(sketch, "E203.MirrorCS", {"start": v(38.82, 35.5) * mm, "end": v(41.36, 35.5) * mm});
            skLineSegment(sketch, "E204.MirrorCS", {"start": v(42.66, 26.95) * mm, "end": v(45.2, 26.95) * mm});
            skLineSegment(sketch, "E205.MirrorCS", {"start": v(54.06, -18.34) * mm, "end": v(56.6, -18.34) * mm});
            skLineSegment(sketch, "E206.MirrorCS", {"start": v(56.6, -60.5) * mm, "end": v(54.06, -60.5) * mm});
            skLineSegment(sketch, "E207.MirrorCS", {"start": v(76.92, -18.34) * mm, "end": v(79.46, -18.34) * mm});
            skLineSegment(sketch, "E208.MirrorCS", {"start": v(46.44, 52.78) * mm, "end": v(48.98, 52.78) * mm});
            skLineSegment(sketch, "E209.MirrorCS", {"start": v(76.92, 16.2) * mm, "end": v(79.46, 16.2) * mm});
            skLineSegment(sketch, "E210.MirrorCS", {"start": v(41.36, 63.5) * mm, "end": v(38.82, 63.5) * mm});
            skLineSegment(sketch, "E211.MirrorCS", {"start": v(61.68, 16.2) * mm, "end": v(64.22, 16.2) * mm});
            skLineSegment(sketch, "E212.MirrorCS", {"start": v(69.3, 16.2) * mm, "end": v(71.84, 16.2) * mm});
            skLineSegment(sketch, "E213.MirrorCS", {"start": v(57.9, -26.4) * mm, "end": v(60.44, -26.4) * mm});
            skLineSegment(sketch, "E214.MirrorCS", {"start": v(57.9, -8.61) * mm, "end": v(60.44, -8.61) * mm});
            skLineSegment(sketch, "E215.MirrorCS", {"start": v(45.84, 65.15) * mm, "end": v(42.03, 65.15) * mm, "construction": true});
            skLineSegment(sketch, "E216.MirrorCS", {"start": v(46.44, -50.85) * mm, "end": v(48.98, -50.85) * mm});
            skLineSegment(sketch, "E217.MirrorCS", {"start": v(65.52, -26.4) * mm, "end": v(68.06, -26.4) * mm});
            skLineSegment(sketch, "E218.MirrorCS", {"start": v(76.92, -1.07) * mm, "end": v(79.46, -1.07) * mm});
            skLineSegment(sketch, "E219.MirrorCS", {"start": v(73.14, -6.07) * mm, "end": v(75.68, -6.07) * mm});
            skLineSegment(sketch, "E220.MirrorCS", {"start": v(73.14, 11.7) * mm, "end": v(75.68, 11.7) * mm});
            skLineSegment(sketch, "E221.MirrorCS", {"start": v(61.68, 35.5) * mm, "end": v(64.22, 35.5) * mm});
            skLineSegment(sketch, "E222.MirrorCS", {"start": v(65.52, -41.63) * mm, "end": v(68.06, -41.63) * mm});
            skLineSegment(sketch, "E223.MirrorCS", {"start": v(61.68, -50.85) * mm, "end": v(64.22, -50.85) * mm});
            skLineSegment(sketch, "E224.MirrorCS", {"start": v(42.66, -26.4) * mm, "end": v(45.2, -26.4) * mm});
            skLineSegment(sketch, "E225.MirrorCS", {"start": v(54.06, -50.85) * mm, "end": v(56.6, -50.85) * mm});
            skLineSegment(sketch, "E226.MirrorCS", {"start": v(50.28, -8.61) * mm, "end": v(52.82, -8.61) * mm});
            skLineSegment(sketch, "E227.MirrorCS", {"start": v(73.14, -59.41) * mm, "end": v(75.68, -59.41) * mm});
            skLineSegment(sketch, "E228.MirrorCS", {"start": v(61.68, -33.58) * mm, "end": v(64.22, -33.58) * mm});
            skLineSegment(sketch, "E229.MirrorCS", {"start": v(65.52, 29.49) * mm, "end": v(68.06, 29.49) * mm});
            skLineSegment(sketch, "E230.MirrorCS", {"start": v(54.06, -52.88) * mm, "end": v(56.6, -52.88) * mm});
            skLineSegment(sketch, "E231.MirrorCS", {"start": v(46.44, -52.88) * mm, "end": v(48.98, -52.88) * mm});
            skLineSegment(sketch, "E232.MirrorCS", {"start": v(50.28, 62.5) * mm, "end": v(52.82, 62.5) * mm});
            skLineSegment(sketch, "E233.MirrorCS", {"start": v(73.14, -8.61) * mm, "end": v(75.68, -8.61) * mm});
            skLineSegment(sketch, "E234.MirrorCS", {"start": v(69.3, -52.88) * mm, "end": v(71.84, -52.88) * mm});
            skLineSegment(sketch, "E235.MirrorCS", {"start": v(71.84, 63.5) * mm, "end": v(69.3, 63.5) * mm});
            skLineSegment(sketch, "E236.MirrorCS", {"start": v(57.9, 29.49) * mm, "end": v(60.44, 29.49) * mm});
            skLineSegment(sketch, "E237.MirrorCS", {"start": v(54.06, 35.5) * mm, "end": v(56.6, 35.5) * mm});
            skLineSegment(sketch, "E238.MirrorCS", {"start": v(73.14, -26.4) * mm, "end": v(75.68, -26.4) * mm});
            skLineSegment(sketch, "E239.MirrorCS", {"start": v(42.66, 44.73) * mm, "end": v(45.2, 44.73) * mm});
            skLineSegment(sketch, "E240.MirrorCS", {"start": v(69.3, 0.97) * mm, "end": v(71.84, 0.97) * mm});
            skLineSegment(sketch, "E241.MirrorCS", {"start": v(61.68, 33.48) * mm, "end": v(64.22, 33.48) * mm});
            skLineSegment(sketch, "E242.MirrorCS", {"start": v(46.44, -33.58) * mm, "end": v(48.98, -33.58) * mm});
            skLineSegment(sketch, "E243.MirrorCS", {"start": v(73.14, 26.95) * mm, "end": v(75.68, 26.95) * mm});
            skLineSegment(sketch, "E244.MirrorCS", {"start": v(69.3, -16.3) * mm, "end": v(71.84, -16.3) * mm});
            skLineSegment(sketch, "E245.MirrorCS", {"start": v(57.9, -6.07) * mm, "end": v(60.44, -6.07) * mm});
            skLineSegment(sketch, "E246.MirrorCS", {"start": v(61.68, -16.3) * mm, "end": v(64.22, -16.3) * mm});
            skLineSegment(sketch, "E247.MirrorCS", {"start": v(42.66, -8.61) * mm, "end": v(45.2, -8.61) * mm});
            skLineSegment(sketch, "E248.MirrorCS", {"start": v(54.06, -33.58) * mm, "end": v(56.6, -33.58) * mm});
            skLineSegment(sketch, "E249.MirrorCS", {"start": v(38.82, 33.48) * mm, "end": v(41.36, 33.48) * mm});
            skLineSegment(sketch, "E250.MirrorCS", {"start": v(54.06, 16.2) * mm, "end": v(56.6, 16.2) * mm});
            skLineSegment(sketch, "E251.MirrorCS", {"start": v(54.06, 50.75) * mm, "end": v(56.6, 50.75) * mm});
            skLineSegment(sketch, "E252.MirrorCS", {"start": v(65.52, 44.73) * mm, "end": v(68.06, 44.73) * mm});
            skLineSegment(sketch, "E253.MirrorCS", {"start": v(79.46, -60.5) * mm, "end": v(76.92, -60.5) * mm});
            skLineSegment(sketch, "E254.MirrorCS", {"start": v(38.82, -1.07) * mm, "end": v(41.36, -1.07) * mm});
            skLineSegment(sketch, "E255.MirrorCS", {"start": v(42.66, -6.07) * mm, "end": v(45.2, -6.07) * mm});
            skLineSegment(sketch, "E256.MirrorCS", {"start": v(76.92, 50.75) * mm, "end": v(79.46, 50.75) * mm});
            skLineSegment(sketch, "E257.MirrorCS", {"start": v(54.06, 18.24) * mm, "end": v(56.6, 18.24) * mm});
            skLineSegment(sketch, "E258.MirrorCS", {"start": v(65.52, 47.27) * mm, "end": v(68.06, 47.27) * mm});
            skLineSegment(sketch, "E259.MirrorCS", {"start": v(73.14, 47.27) * mm, "end": v(75.68, 47.27) * mm});
            skLineSegment(sketch, "E260.MirrorCS", {"start": v(76.92, 52.78) * mm, "end": v(79.46, 52.78) * mm});
            skLineSegment(sketch, "E261.MirrorCS", {"start": v(61.68, -35.61) * mm, "end": v(64.22, -35.61) * mm});
            skLineSegment(sketch, "E262.MirrorCS", {"start": v(57.9, 9.17) * mm, "end": v(60.44, 9.17) * mm});
            skLineSegment(sketch, "E263.MirrorCS", {"start": v(38.82, 50.75) * mm, "end": v(41.36, 50.75) * mm});
            skLineSegment(sketch, "E264.MirrorCS", {"start": v(54.06, 0.97) * mm, "end": v(56.6, 0.97) * mm});
            skLineSegment(sketch, "E265.MirrorCS", {"start": v(46.44, 33.48) * mm, "end": v(48.98, 33.48) * mm});
            skLineSegment(sketch, "E266.MirrorCS", {"start": v(46.44, -1.07) * mm, "end": v(48.98, -1.07) * mm});
            skLineSegment(sketch, "E267.MirrorCS", {"start": v(42.66, 29.49) * mm, "end": v(45.2, 29.49) * mm});
            skLineSegment(sketch, "E268.MirrorCS", {"start": v(73.14, 62.5) * mm, "end": v(75.68, 62.5) * mm});
            skLineSegment(sketch, "E269.MirrorCS", {"start": v(61.68, 18.24) * mm, "end": v(64.22, 18.24) * mm});
            skLineSegment(sketch, "E270.MirrorCS", {"start": v(46.44, 50.75) * mm, "end": v(48.98, 50.75) * mm});
            skLineSegment(sketch, "E271.MirrorCS", {"start": v(65.52, -8.61) * mm, "end": v(68.06, -8.61) * mm});
            skLineSegment(sketch, "E272.MirrorCS", {"start": v(76.92, -33.58) * mm, "end": v(79.46, -33.58) * mm});
            skLineSegment(sketch, "E273.MirrorCS", {"start": v(65.52, -6.07) * mm, "end": v(68.06, -6.07) * mm});
            skLineSegment(sketch, "E274.MirrorCS", {"start": v(57.9, 26.95) * mm, "end": v(60.44, 26.95) * mm});
            skLineSegment(sketch, "E275.MirrorCS", {"start": v(38.82, -35.61) * mm, "end": v(41.36, -35.61) * mm});
            skLineSegment(sketch, "E276.MirrorCS", {"start": v(45.2, 62.5) * mm, "end": v(45.2, 47.27) * mm});
            skLineSegment(sketch, "E277.MirrorCS", {"start": v(71.84, 50.75) * mm, "end": v(71.84, 35.5) * mm});
            skLineSegment(sketch, "E278.MirrorCS", {"start": v(69.3, 50.75) * mm, "end": v(69.3, 35.5) * mm});
            skLineSegment(sketch, "E279.MirrorCS", {"start": v(42.66, 44.73) * mm, "end": v(42.66, 29.49) * mm});
            skLineSegment(sketch, "E280.MirrorCS", {"start": v(46.44, 50.75) * mm, "end": v(46.44, 35.5) * mm});
            skLineSegment(sketch, "E281.MirrorCS", {"start": v(54.06, 63.5) * mm, "end": v(54.06, 52.78) * mm});
            skLineSegment(sketch, "E282.MirrorCS", {"start": v(45.2, 44.73) * mm, "end": v(45.2, 29.49) * mm});
            skLineSegment(sketch, "E283.MirrorCS", {"start": v(54.06, 50.75) * mm, "end": v(54.06, 35.5) * mm});
            skLineSegment(sketch, "E284.MirrorCS", {"start": v(57.9, 44.73) * mm, "end": v(57.9, 29.49) * mm});
            skLineSegment(sketch, "E285.MirrorCS", {"start": v(56.6, 63.5) * mm, "end": v(56.6, 52.78) * mm});
            skLineSegment(sketch, "E286.MirrorCS", {"start": v(57.9, 62.5) * mm, "end": v(57.9, 47.27) * mm});
            skLineSegment(sketch, "E287.MirrorCS", {"start": v(60.44, 62.5) * mm, "end": v(60.44, 47.27) * mm});
            skLineSegment(sketch, "E288.MirrorCS", {"start": v(60.44, 44.73) * mm, "end": v(60.44, 29.49) * mm});
            skLineSegment(sketch, "E289.MirrorCS", {"start": v(42.66, 62.5) * mm, "end": v(42.66, 47.27) * mm});
            skLineSegment(sketch, "E290.MirrorCS", {"start": v(45.2, -44.17) * mm, "end": v(45.2, -59.41) * mm});
            skLineSegment(sketch, "E291.MirrorCS", {"start": v(69.3, 63.5) * mm, "end": v(69.3, 52.78) * mm});
            skLineSegment(sketch, "E292.MirrorCS", {"start": v(41.36, -52.88) * mm, "end": v(41.36, -60.5) * mm});
            skLineSegment(sketch, "E293.MirrorCS", {"start": v(56.6, 50.75) * mm, "end": v(56.6, 35.5) * mm});
            skLineSegment(sketch, "E294.MirrorCS", {"start": v(46.44, 63.5) * mm, "end": v(46.44, 52.78) * mm});
            skLineSegment(sketch, "E295.MirrorCS", {"start": v(71.84, 63.5) * mm, "end": v(71.84, 52.78) * mm});
            skPoint(sketch, "E296.MirrorP", {"position": v(59.17, -16.23) * mm});
            skPoint(sketch, "E297.MirrorP", {"position": v(55.33, -8.69) * mm});
            skLineSegment(sketch, "E298.MirrorCS", {"start": v(69.3, -35.61) * mm, "end": v(69.3, -50.85) * mm});
            skLineSegment(sketch, "E299.MirrorCS", {"start": v(73.14, 9.17) * mm, "end": v(73.14, -6.07) * mm});
            skPoint(sketch, "E300.MirrorP", {"position": v(55.33, -43.23) * mm});
            skLineSegment(sketch, "E301.MirrorCS", {"start": v(75.68, 62.5) * mm, "end": v(75.68, 47.27) * mm});
            skLineSegment(sketch, "E302.MirrorCS", {"start": v(68.06, 9.17) * mm, "end": v(68.06, -6.07) * mm});
            skPoint(sketch, "E303.MirrorP", {"position": v(62.95, 43.13) * mm});
            skLineSegment(sketch, "E304.MirrorCS", {"start": v(42.66, -26.4) * mm, "end": v(42.66, -41.63) * mm});
            skPoint(sketch, "E305.MirrorP", {"position": v(78.2, -60.5) * mm});
            skLineSegment(sketch, "E306.MirrorCS", {"start": v(65.52, -44.17) * mm, "end": v(65.52, -59.41) * mm});
            skLineSegment(sketch, "E307.MirrorCS", {"start": v(50.28, -44.17) * mm, "end": v(50.28, -59.41) * mm});
            skLineSegment(sketch, "E308.MirrorCS", {"start": v(52.82, -8.61) * mm, "end": v(52.82, -23.85) * mm});
            skLineSegment(sketch, "E309.MirrorCS", {"start": v(50.28, -26.4) * mm, "end": v(50.28, -41.63) * mm});
            skLineSegment(sketch, "E310.MirrorCS", {"start": v(38.82, 50.75) * mm, "end": v(38.82, 35.5) * mm});
            skLineSegment(sketch, "E311.MirrorCS", {"start": v(56.6, -35.61) * mm, "end": v(56.6, -50.85) * mm});
            skPoint(sketch, "E312.MirrorP", {"position": v(43.93, 37.1) * mm});
            skLineSegment(sketch, "E313.MirrorCS", {"start": v(38.82, 33.48) * mm, "end": v(38.82, 18.24) * mm});
            skPoint(sketch, "E314.MirrorP", {"position": v(51.55, 1.55) * mm});
            skPoint(sketch, "E315.MirrorP", {"position": v(43.93, -34.01) * mm});
            skLineSegment(sketch, "E316.MirrorCS", {"start": v(45.2, -26.4) * mm, "end": v(45.2, -41.63) * mm});
            skLineSegment(sketch, "E317.MirrorCS", {"start": v(42.66, -44.17) * mm, "end": v(42.66, -59.41) * mm});
            skPoint(sketch, "E318.MirrorP", {"position": v(43.93, -16.23) * mm});
            skLineSegment(sketch, "E319.MirrorCS", {"start": v(38.82, -52.88) * mm, "end": v(38.82, -60.5) * mm});
            skPoint(sketch, "E320.MirrorP", {"position": v(43.93, 1.55) * mm});
            skLineSegment(sketch, "E321.MirrorCS", {"start": v(54.06, -1.07) * mm, "end": v(54.06, -16.3) * mm});
            skLineSegment(sketch, "E322.MirrorCS", {"start": v(76.92, 16.2) * mm, "end": v(76.92, 0.97) * mm});
            skPoint(sketch, "E323.MirrorP", {"position": v(59.17, 54.89) * mm});
            skPoint(sketch, "E324.MirrorP", {"position": v(74.41, 37.1) * mm});
            skPoint(sketch, "E325.MirrorP", {"position": v(47.71, 8.59) * mm});
            skLineSegment(sketch, "E326.MirrorCS", {"start": v(56.6, 16.2) * mm, "end": v(56.6, 0.97) * mm});
            skLineSegment(sketch, "E327.MirrorCS", {"start": v(48.98, 50.75) * mm, "end": v(48.98, 35.5) * mm});
            skPoint(sketch, "E328.MirrorP", {"position": v(70.57, -60.5) * mm});
            skLineSegment(sketch, "E329.MirrorCS", {"start": v(64.22, -35.61) * mm, "end": v(64.22, -50.85) * mm});
            skLineSegment(sketch, "E330.MirrorCS", {"start": v(79.46, 33.48) * mm, "end": v(79.46, 18.24) * mm});
            skPoint(sketch, "E331.MirrorP", {"position": v(47.71, 60.4) * mm});
            skPoint(sketch, "E332.MirrorP", {"position": v(51.55, 19.33) * mm});
            skPoint(sketch, "E333.MirrorP", {"position": v(70.57, 25.86) * mm});
            skPoint(sketch, "E334.MirrorP", {"position": v(62.95, -8.69) * mm});
            skPoint(sketch, "E335.MirrorP", {"position": v(43.93, 54.89) * mm});
            skLineSegment(sketch, "E336.MirrorCS", {"start": v(79.46, -18.34) * mm, "end": v(79.46, -33.58) * mm});
            skLineSegment(sketch, "E337.MirrorCS", {"start": v(64.22, 33.48) * mm, "end": v(64.22, 18.24) * mm});
            skLineSegment(sketch, "E338.MirrorCS", {"start": v(61.68, -18.34) * mm, "end": v(61.68, -33.58) * mm});
            skLineSegment(sketch, "E339.MirrorCS", {"start": v(56.6, -1.07) * mm, "end": v(56.6, -16.3) * mm});
            skLineSegment(sketch, "E340.MirrorCS", {"start": v(38.82, -35.61) * mm, "end": v(38.82, -50.85) * mm});
            skLineSegment(sketch, "E341.MirrorCS", {"start": v(69.3, 33.48) * mm, "end": v(69.3, 18.24) * mm});
            skPoint(sketch, "E342.MirrorP", {"position": v(40.1, -43.23) * mm});
            skLineSegment(sketch, "E343.MirrorCS", {"start": v(57.9, -26.4) * mm, "end": v(57.9, -41.63) * mm});
            skLineSegment(sketch, "E344.MirrorCS", {"start": v(68.06, 62.5) * mm, "end": v(68.06, 47.27) * mm});
            skLineSegment(sketch, "E345.MirrorCS", {"start": v(48.98, -52.88) * mm, "end": v(48.98, -60.5) * mm});
            skPoint(sketch, "E346.MirrorP", {"position": v(51.55, -51.8) * mm});
            skLineSegment(sketch, "E347.MirrorCS", {"start": v(56.6, -52.88) * mm, "end": v(56.6, -60.5) * mm});
            skLineSegment(sketch, "E348.MirrorCS", {"start": v(38.82, -1.07) * mm, "end": v(38.82, -16.3) * mm});
            skLineSegment(sketch, "E349.MirrorCS", {"start": v(46.44, -35.61) * mm, "end": v(46.44, -50.85) * mm});
            skLineSegment(sketch, "E350.MirrorCS", {"start": v(42.66, 26.95) * mm, "end": v(42.66, 11.7) * mm});
            skLineSegment(sketch, "E351.MirrorCS", {"start": v(41.36, 16.2) * mm, "end": v(41.36, 0.97) * mm});
            skLineSegment(sketch, "E352.MirrorCS", {"start": v(46.44, -52.88) * mm, "end": v(46.44, -60.5) * mm});
            skLineSegment(sketch, "E353.MirrorCS", {"start": v(48.98, 33.48) * mm, "end": v(48.98, 18.24) * mm});
            skPoint(sketch, "E354.MirrorP", {"position": v(51.55, -34.01) * mm});
            skPoint(sketch, "E355.MirrorP", {"position": v(74.41, -16.23) * mm});
            skPoint(sketch, "E356.MirrorP", {"position": v(51.55, 54.89) * mm});
            skLineSegment(sketch, "E357.MirrorCS", {"start": v(45.2, -59.41) * mm, "end": v(45.2, -41.63) * mm, "construction": true});
            skPoint(sketch, "E358.MirrorP", {"position": v(70.57, -8.69) * mm});
            skLineSegment(sketch, "E359.MirrorCS", {"start": v(54.06, -18.34) * mm, "end": v(54.06, -33.58) * mm});
            skLineSegment(sketch, "E360.MirrorCS", {"start": v(68.06, -44.17) * mm, "end": v(68.06, -59.41) * mm});
            skPoint(sketch, "E361.MirrorP", {"position": v(51.55, 37.1) * mm});
            skLineSegment(sketch, "E362.MirrorCS", {"start": v(65.52, 26.95) * mm, "end": v(65.52, 11.7) * mm});
            skLineSegment(sketch, "E363.MirrorCS", {"start": v(38.82, -18.34) * mm, "end": v(38.82, -33.58) * mm});
            skLineSegment(sketch, "E364.MirrorCS", {"start": v(79.46, -35.61) * mm, "end": v(79.46, -50.85) * mm});
            skLineSegment(sketch, "E365.MirrorCS", {"start": v(64.22, 50.75) * mm, "end": v(64.22, 35.5) * mm});
            skLineSegment(sketch, "E366.MirrorCS", {"start": v(71.84, -1.07) * mm, "end": v(71.84, -16.3) * mm});
            skPoint(sketch, "E367.MirrorP", {"position": v(78.2, -8.69) * mm});
            skPoint(sketch, "E368.MirrorP", {"position": v(47.71, -25.96) * mm});
            skPoint(sketch, "E369.MirrorP", {"position": v(70.57, -43.23) * mm});
            skLineSegment(sketch, "E370.MirrorCS", {"start": v(60.44, -44.17) * mm, "end": v(60.44, -59.41) * mm});
            skLineSegment(sketch, "E371.MirrorCS", {"start": v(38.82, 63.5) * mm, "end": v(38.82, 52.78) * mm});
            skPoint(sketch, "E372.MirrorP", {"position": v(40.1, 43.13) * mm});
            skPoint(sketch, "E373.MirrorP", {"position": v(55.33, 60.4) * mm});
            skPoint(sketch, "E374.MirrorP", {"position": v(40.1, 8.59) * mm});
            skPoint(sketch, "E375.MirrorP", {"position": v(78.2, 60.4) * mm});
            skLineSegment(sketch, "E376.MirrorCS", {"start": v(65.52, 44.73) * mm, "end": v(65.52, 29.49) * mm});
            skLineSegment(sketch, "E377.MirrorCS", {"start": v(57.9, -44.17) * mm, "end": v(57.9, -59.41) * mm});
            skLineSegment(sketch, "E378.MirrorCS", {"start": v(76.92, 33.48) * mm, "end": v(76.92, 18.24) * mm});
            skPoint(sketch, "E379.MirrorP", {"position": v(78.2, 25.86) * mm});
            skPoint(sketch, "E380.MirrorP", {"position": v(66.8, 37.1) * mm});
            skLineSegment(sketch, "E381.MirrorCS", {"start": v(42.66, -8.61) * mm, "end": v(42.66, -23.85) * mm});
            skLineSegment(sketch, "E382.MirrorCS", {"start": v(52.82, 26.95) * mm, "end": v(52.82, 11.7) * mm});
            skLineSegment(sketch, "E383.MirrorCS", {"start": v(61.68, 50.75) * mm, "end": v(61.68, 35.5) * mm});
            skLineSegment(sketch, "E384.MirrorCS", {"start": v(65.52, 9.17) * mm, "end": v(65.52, -6.07) * mm});
            skLineSegment(sketch, "E385.MirrorCS", {"start": v(56.6, -18.34) * mm, "end": v(56.6, -33.58) * mm});
            skLineSegment(sketch, "E386.MirrorCS", {"start": v(52.82, 9.17) * mm, "end": v(52.82, -6.07) * mm});
            skLineSegment(sketch, "E387.MirrorCS", {"start": v(60.44, -8.61) * mm, "end": v(60.44, -23.85) * mm});
            skLineSegment(sketch, "E388.MirrorCS", {"start": v(71.84, 16.2) * mm, "end": v(71.84, 0.97) * mm});
            skPoint(sketch, "E389.MirrorP", {"position": v(66.8, -34.01) * mm});
            skPoint(sketch, "E390.MirrorP", {"position": v(59.17, -51.8) * mm});
            skLineSegment(sketch, "E391.MirrorCS", {"start": v(46.44, 16.2) * mm, "end": v(46.44, 0.97) * mm});
            skPoint(sketch, "E392.MirrorP", {"position": v(78.2, -25.96) * mm});
            skLineSegment(sketch, "E393.MirrorCS", {"start": v(50.28, 62.5) * mm, "end": v(50.28, 47.27) * mm});
            skLineSegment(sketch, "E394.MirrorCS", {"start": v(71.84, -35.61) * mm, "end": v(71.84, -50.85) * mm});
            skLineSegment(sketch, "E395.MirrorCS", {"start": v(41.36, 50.75) * mm, "end": v(41.36, 35.5) * mm});
            skPoint(sketch, "E396.MirrorP", {"position": v(59.17, 19.33) * mm});
            skPoint(sketch, "E397.MirrorP", {"position": v(55.33, -25.96) * mm});
            skLineSegment(sketch, "E398.MirrorCS", {"start": v(60.44, 26.95) * mm, "end": v(60.44, 11.7) * mm});
            skPoint(sketch, "E399.MirrorP", {"position": v(62.95, -60.5) * mm});
            skLineSegment(sketch, "E400.MirrorCS", {"start": v(69.3, 16.2) * mm, "end": v(69.3, 0.97) * mm});
            skLineSegment(sketch, "E401.MirrorCS", {"start": v(69.3, -1.07) * mm, "end": v(69.3, -16.3) * mm});
            skLineSegment(sketch, "E402.MirrorCS", {"start": v(48.98, 63.5) * mm, "end": v(48.98, 52.78) * mm});
            skLineSegment(sketch, "E403.MirrorCS", {"start": v(48.98, 16.2) * mm, "end": v(48.98, 0.97) * mm});
            skLineSegment(sketch, "E404.MirrorCS", {"start": v(61.68, 63.5) * mm, "end": v(61.68, 52.78) * mm});
            skLineSegment(sketch, "E405.MirrorCS", {"start": v(52.82, -44.17) * mm, "end": v(52.82, -59.41) * mm});
            skLineSegment(sketch, "E406.MirrorCS", {"start": v(64.22, 16.2) * mm, "end": v(64.22, 0.97) * mm});
            skLineSegment(sketch, "E407.MirrorCS", {"start": v(71.84, -18.34) * mm, "end": v(71.84, -33.58) * mm});
            skLineSegment(sketch, "E408.MirrorCS", {"start": v(68.06, 26.95) * mm, "end": v(68.06, 11.7) * mm});
            skLineSegment(sketch, "E409.MirrorCS", {"start": v(61.68, -52.88) * mm, "end": v(61.68, -60.5) * mm});
            skLineSegment(sketch, "E410.MirrorCS", {"start": v(69.3, -18.34) * mm, "end": v(69.3, -33.58) * mm});
            skPoint(sketch, "E411.MirrorP", {"position": v(66.8, -16.23) * mm});
            skLineSegment(sketch, "E412.MirrorCS", {"start": v(52.82, 62.5) * mm, "end": v(52.82, 47.27) * mm});
            skPoint(sketch, "E413.MirrorP", {"position": v(66.8, 54.89) * mm});
            skLineSegment(sketch, "E414.MirrorCS", {"start": v(41.36, -60.5) * mm, "end": v(41.36, -50.85) * mm, "construction": true});
            skPoint(sketch, "E415.MirrorP", {"position": v(62.95, -43.23) * mm});
            skLineSegment(sketch, "E416.MirrorCS", {"start": v(76.92, -18.34) * mm, "end": v(76.92, -33.58) * mm});
            skLineSegment(sketch, "E417.MirrorCS", {"start": v(42.66, 9.17) * mm, "end": v(42.66, -6.07) * mm});
            skPoint(sketch, "E418.MirrorP", {"position": v(40.1, -25.96) * mm});
            skLineSegment(sketch, "E419.MirrorCS", {"start": v(54.06, 33.48) * mm, "end": v(54.06, 18.24) * mm});
            skPoint(sketch, "E420.MirrorP", {"position": v(59.17, 37.1) * mm});
            skLineSegment(sketch, "E421.MirrorCS", {"start": v(54.06, -35.61) * mm, "end": v(54.06, -50.85) * mm});
            skLineSegment(sketch, "E422.MirrorCS", {"start": v(64.22, -1.07) * mm, "end": v(64.22, -16.3) * mm});
            skLineSegment(sketch, "E423.MirrorCS", {"start": v(79.46, 63.5) * mm, "end": v(79.46, 52.78) * mm});
            skPoint(sketch, "E424.MirrorP", {"position": v(43.93, 19.33) * mm});
            skLineSegment(sketch, "E425.MirrorCS", {"start": v(52.82, 44.73) * mm, "end": v(52.82, 29.49) * mm});
            skLineSegment(sketch, "E426.MirrorCS", {"start": v(48.98, -35.61) * mm, "end": v(48.98, -50.85) * mm});
            skPoint(sketch, "E427.MirrorP", {"position": v(70.57, 60.4) * mm});
            skLineSegment(sketch, "E428.MirrorCS", {"start": v(54.06, -52.88) * mm, "end": v(54.06, -60.5) * mm});
            skPoint(sketch, "E429.MirrorP", {"position": v(62.95, 25.86) * mm});
            skLineSegment(sketch, "E430.MirrorCS", {"start": v(45.2, 26.95) * mm, "end": v(45.2, 11.7) * mm});
            skPoint(sketch, "E431.MirrorP", {"position": v(74.41, 1.55) * mm});
            skLineSegment(sketch, "E432.MirrorCS", {"start": v(50.28, 26.95) * mm, "end": v(50.28, 11.7) * mm});
            skPoint(sketch, "E433.MirrorP", {"position": v(59.17, -34.01) * mm});
            skLineSegment(sketch, "E434.MirrorCS", {"start": v(76.92, -35.61) * mm, "end": v(76.92, -50.85) * mm});
            skLineSegment(sketch, "E435.MirrorCS", {"start": v(64.22, -52.88) * mm, "end": v(64.22, -60.5) * mm});
            skLineSegment(sketch, "E436.MirrorCS", {"start": v(46.44, 33.48) * mm, "end": v(46.44, 18.24) * mm});
            skLineSegment(sketch, "E437.MirrorCS", {"start": v(50.28, 44.73) * mm, "end": v(50.28, 29.49) * mm});
            skLineSegment(sketch, "E438.MirrorCS", {"start": v(56.6, 33.48) * mm, "end": v(56.6, 18.24) * mm});
            skPoint(sketch, "E439.MirrorP", {"position": v(47.71, 25.86) * mm});
            skLineSegment(sketch, "E440.MirrorCS", {"start": v(65.52, 62.5) * mm, "end": v(65.52, 47.27) * mm});
            skLineSegment(sketch, "E441.MirrorCS", {"start": v(41.36, 33.48) * mm, "end": v(41.36, 18.24) * mm});
            skLineSegment(sketch, "E442.MirrorCS", {"start": v(73.14, -44.17) * mm, "end": v(73.14, -59.41) * mm});
            skPoint(sketch, "E443.MirrorP", {"position": v(43.93, -51.8) * mm});
            skPoint(sketch, "E444.MirrorP", {"position": v(62.95, 60.4) * mm});
            skPoint(sketch, "E445.MirrorP", {"position": v(78.2, -43.23) * mm});
            skLineSegment(sketch, "E446.MirrorCS", {"start": v(68.06, 44.73) * mm, "end": v(68.06, 29.49) * mm});
            skLineSegment(sketch, "E447.MirrorCS", {"start": v(57.9, 9.17) * mm, "end": v(57.9, -6.07) * mm});
            skLineSegment(sketch, "E448.MirrorCS", {"start": v(41.36, -18.34) * mm, "end": v(41.36, -33.58) * mm});
            skPoint(sketch, "E449.MirrorP", {"position": v(47.71, -43.23) * mm});
            skPoint(sketch, "E450.MirrorP", {"position": v(51.55, -16.23) * mm});
            skLineSegment(sketch, "E451.MirrorCS", {"start": v(45.2, -8.61) * mm, "end": v(45.2, -23.85) * mm});
            skLineSegment(sketch, "E452.MirrorCS", {"start": v(54.06, 16.2) * mm, "end": v(54.06, 0.97) * mm});
            skPoint(sketch, "E453.MirrorP", {"position": v(62.95, 8.59) * mm});
            skLineSegment(sketch, "E454.MirrorCS", {"start": v(79.46, 16.2) * mm, "end": v(79.46, 0.97) * mm});
            skLineSegment(sketch, "E455.MirrorCS", {"start": v(57.9, 26.95) * mm, "end": v(57.9, 11.7) * mm});
            skPoint(sketch, "E456.MirrorP", {"position": v(59.17, 1.55) * mm});
            skPoint(sketch, "E457.MirrorP", {"position": v(74.41, 54.89) * mm});
            skPoint(sketch, "E458.MirrorP", {"position": v(47.71, -8.69) * mm});
            skLineSegment(sketch, "E459.MirrorCS", {"start": v(48.98, -1.07) * mm, "end": v(48.98, -16.3) * mm});
            skLineSegment(sketch, "E460.MirrorCS", {"start": v(46.44, -1.07) * mm, "end": v(46.44, -16.3) * mm});
            skLineSegment(sketch, "E461.MirrorCS", {"start": v(76.92, 63.5) * mm, "end": v(76.92, 52.78) * mm});
            skLineSegment(sketch, "E462.MirrorCS", {"start": v(41.36, -35.61) * mm, "end": v(41.36, -50.85) * mm});
            skLineSegment(sketch, "E463.MirrorCS", {"start": v(76.92, -1.07) * mm, "end": v(76.92, -16.3) * mm});
            skLineSegment(sketch, "E464.MirrorCS", {"start": v(68.06, -26.4) * mm, "end": v(68.06, -41.63) * mm});
            skPoint(sketch, "E465.MirrorP", {"position": v(74.41, 19.33) * mm});
            skPoint(sketch, "E466.MirrorP", {"position": v(40.1, -8.69) * mm});
            skLineSegment(sketch, "E467.MirrorCS", {"start": v(75.68, 26.95) * mm, "end": v(75.68, 11.7) * mm});
            skLineSegment(sketch, "E468.MirrorCS", {"start": v(71.84, -52.88) * mm, "end": v(71.84, -60.5) * mm});
            skLineSegment(sketch, "E469.MirrorCS", {"start": v(64.22, 63.5) * mm, "end": v(64.22, 52.78) * mm});
            skPoint(sketch, "E470.MirrorP", {"position": v(78.2, 43.13) * mm});
            skLineSegment(sketch, "E471.MirrorCS", {"start": v(71.84, 33.48) * mm, "end": v(71.84, 18.24) * mm});
            skLineSegment(sketch, "E472.MirrorCS", {"start": v(73.14, 44.73) * mm, "end": v(73.14, 29.49) * mm});
            skPoint(sketch, "E473.MirrorP", {"position": v(55.33, 25.86) * mm});
            skPoint(sketch, "E474.MirrorP", {"position": v(66.8, 1.55) * mm});
            skPoint(sketch, "E475.MirrorP", {"position": v(70.57, -25.96) * mm});
            skLineSegment(sketch, "E476.MirrorCS", {"start": v(60.44, -26.4) * mm, "end": v(60.44, -41.63) * mm});
            skPoint(sketch, "E477.MirrorP", {"position": v(66.8, 19.33) * mm});
            skLineSegment(sketch, "E478.MirrorCS", {"start": v(50.28, -8.61) * mm, "end": v(50.28, -23.85) * mm});
            skLineSegment(sketch, "E479.MirrorCS", {"start": v(73.14, 62.5) * mm, "end": v(73.14, 47.27) * mm});
            skLineSegment(sketch, "E480.MirrorCS", {"start": v(75.68, -8.61) * mm, "end": v(75.68, -23.85) * mm});
            skLineSegment(sketch, "E481.MirrorCS", {"start": v(65.52, -8.61) * mm, "end": v(65.52, -23.85) * mm});
            skPoint(sketch, "E482.MirrorP", {"position": v(47.71, -60.5) * mm});
            skLineSegment(sketch, "E483.MirrorCS", {"start": v(75.68, -26.4) * mm, "end": v(75.68, -41.63) * mm});
            skLineSegment(sketch, "E484.MirrorCS", {"start": v(73.14, -26.4) * mm, "end": v(73.14, -41.63) * mm});
            skPoint(sketch, "E485.MirrorP", {"position": v(47.71, 43.13) * mm});
            skPoint(sketch, "E486.MirrorP", {"position": v(78.2, 8.59) * mm});
            skLineSegment(sketch, "E487.MirrorCS", {"start": v(68.06, -8.61) * mm, "end": v(68.06, -23.85) * mm});
            skLineSegment(sketch, "E488.MirrorCS", {"start": v(75.68, 9.17) * mm, "end": v(75.68, -6.07) * mm});
            skLineSegment(sketch, "E489.MirrorCS", {"start": v(61.68, -1.07) * mm, "end": v(61.68, -16.3) * mm});
            skPoint(sketch, "E490.MirrorP", {"position": v(55.33, -60.5) * mm});
            skLineSegment(sketch, "E491.MirrorCS", {"start": v(79.46, 50.75) * mm, "end": v(79.46, 35.5) * mm});
            skLineSegment(sketch, "E492.MirrorCS", {"start": v(76.92, -52.88) * mm, "end": v(76.92, -60.5) * mm});
            skLineSegment(sketch, "E493.MirrorCS", {"start": v(57.9, -8.61) * mm, "end": v(57.9, -23.85) * mm});
            skLineSegment(sketch, "E494.MirrorCS", {"start": v(60.44, 9.17) * mm, "end": v(60.44, -6.07) * mm});
            skPoint(sketch, "E495.MirrorP", {"position": v(40.1, 60.4) * mm});
            skPoint(sketch, "E496.MirrorP", {"position": v(55.33, 43.13) * mm});
            skPoint(sketch, "E497.MirrorP", {"position": v(40.1, -60.5) * mm});
            skPoint(sketch, "E498.MirrorP", {"position": v(55.33, 8.59) * mm});
            skLineSegment(sketch, "E499.MirrorCS", {"start": v(41.36, -1.07) * mm, "end": v(41.36, -16.3) * mm});
            skLineSegment(sketch, "E500.MirrorCS", {"start": v(41.36, 63.5) * mm, "end": v(41.36, 52.78) * mm});
            skLineSegment(sketch, "E501.MirrorCS", {"start": v(79.46, -1.07) * mm, "end": v(79.46, -16.3) * mm});
            skLineSegment(sketch, "E502.MirrorCS", {"start": v(75.68, 44.73) * mm, "end": v(75.68, 29.49) * mm});
            skPoint(sketch, "E503.MirrorP", {"position": v(70.57, 8.59) * mm});
            skLineSegment(sketch, "E504.MirrorCS", {"start": v(65.52, -26.4) * mm, "end": v(65.52, -41.63) * mm});
            skLineSegment(sketch, "E505.MirrorCS", {"start": v(38.82, 16.2) * mm, "end": v(38.82, 0.97) * mm});
            skPoint(sketch, "E506.MirrorP", {"position": v(74.41, -51.8) * mm});
            skLineSegment(sketch, "E507.MirrorCS", {"start": v(61.68, 33.48) * mm, "end": v(61.68, 18.24) * mm});
            skLineSegment(sketch, "E508.MirrorCS", {"start": v(75.68, -44.17) * mm, "end": v(75.68, -59.41) * mm});
            skLineSegment(sketch, "E509.MirrorCS", {"start": v(64.22, -18.34) * mm, "end": v(64.22, -33.58) * mm});
            skLineSegment(sketch, "E510.MirrorCS", {"start": v(46.44, -18.34) * mm, "end": v(46.44, -33.58) * mm});
            skPoint(sketch, "E511.MirrorP", {"position": v(74.41, -34.01) * mm});
            skLineSegment(sketch, "E512.MirrorCS", {"start": v(61.68, -35.61) * mm, "end": v(61.68, -50.85) * mm});
            skLineSegment(sketch, "E513.MirrorCS", {"start": v(76.92, 50.75) * mm, "end": v(76.92, 35.5) * mm});
            skPoint(sketch, "E514.MirrorP", {"position": v(70.57, 43.13) * mm});
            skLineSegment(sketch, "E515.MirrorCS", {"start": v(48.98, -18.34) * mm, "end": v(48.98, -33.58) * mm});
            skPoint(sketch, "E516.MirrorP", {"position": v(40.1, 25.86) * mm});
            skLineSegment(sketch, "E517.MirrorCS", {"start": v(69.3, -52.88) * mm, "end": v(69.3, -60.5) * mm});
            skPoint(sketch, "E518.MirrorP", {"position": v(66.8, -51.8) * mm});
            skLineSegment(sketch, "E519.MirrorCS", {"start": v(45.2, 9.17) * mm, "end": v(45.2, -6.07) * mm});
            skLineSegment(sketch, "E520.MirrorCS", {"start": v(50.28, 9.17) * mm, "end": v(50.28, -6.07) * mm});
            skLineSegment(sketch, "E521.MirrorCS", {"start": v(73.14, -8.61) * mm, "end": v(73.14, -23.85) * mm});
            skLineSegment(sketch, "E522.MirrorCS", {"start": v(52.82, -26.4) * mm, "end": v(52.82, -41.63) * mm});
            skLineSegment(sketch, "E523.MirrorCS", {"start": v(61.68, 16.2) * mm, "end": v(61.68, 0.97) * mm});
            skPoint(sketch, "E524.MirrorP", {"position": v(62.95, -25.96) * mm});
            skLineSegment(sketch, "E525.MirrorCS", {"start": v(79.46, -52.88) * mm, "end": v(79.46, -60.5) * mm});
            skLineSegment(sketch, "E526.MirrorCS", {"start": v(43.93, 65.15) * mm, "end": v(43.93, 48.68) * mm, "construction": true});
            skLineSegment(sketch, "E527.MirrorCS", {"start": v(73.14, 26.95) * mm, "end": v(73.14, 11.7) * mm});
            skSolve(sketch);
        }
        {
            var Q0;
            Q0 = qSketchRegion(id + "F2", true);
            extrude(context, id + "F3", {"entities" : qUnion([Q0]), "operationType" : NewBodyOperationType.REMOVE, "endBound" : BoundingType.THROUGH_ALL, "oppositeDirection" : true, "depth" : 25.4 * mm, "offsetDistance" : 25.4 * mm});
        }
    });
